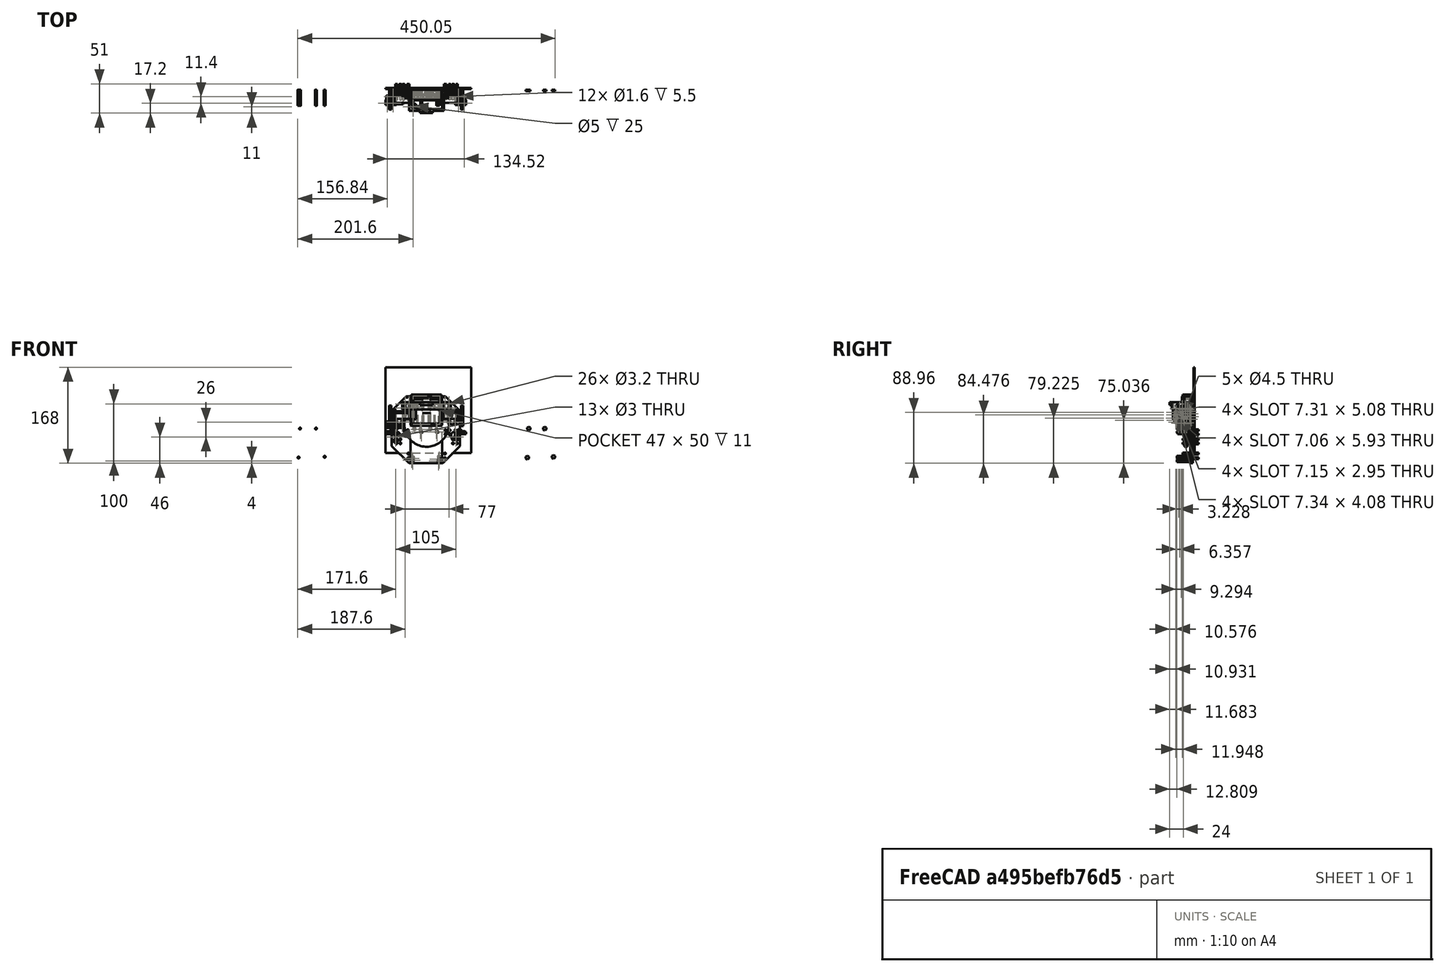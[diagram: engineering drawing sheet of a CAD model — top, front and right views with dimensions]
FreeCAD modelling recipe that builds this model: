
FCSTD DOCUMENT  (FreeCAD 0.17R13522 (Git))
Label: 5028.6 Frank
License: All rights reserved
LicenseURL: http://en.wikipedia.org/wiki/All_rights_reserved
objects: Part::Cylinder×153, Part::Fuse×90, Part::Box×86, Part::Cut×84, Part::Feature×37, Part::MultiFuse×35, Part::Fillet×28, Part::Chamfer×25, Part::Mirroring×16, Part::Cone×12, Part::Compound×3, Part::Torus×2, App::DocumentObjectGroup×1
note: 571 computed .brp shape members not serialized (recipe doc carries the construction recipe); baked Part::Feature solids carry a one-line shape summary decoded from their .brp

FEATURE [Part::Cylinder] Cylinder
  Angle = 360
  AttacherType = Attacher::AttachEngine3D
  Height = 30
  Radius = 7
FEATURE [Part::Cylinder] Cylinder001
  Angle = 360
  AttacherType = Attacher::AttachEngine3D
  Height = 19
  Placement = pos=(0,0,30) rot=(0,0,1;0rad)
  Radius = 7
FEATURE [Part::Cylinder] Cylinder002
  Angle = 360
  AttacherType = Attacher::AttachEngine3D
  Height = 1.8
  Placement = pos=(0,0,49) rot=(0,0,1;0rad)
  Radius = 2.5
FEATURE [Part::Compound] Compound
  Links = -> [Cylinder,Cylinder002,Cylinder001]
FEATURE [Part::Cylinder] Cylinder003
  Angle = 360
  AttacherType = Attacher::AttachEngine3D
  Height = 30
  Radius = 7
FEATURE [Part::Cylinder] Cylinder004
  Angle = 360
  AttacherType = Attacher::AttachEngine3D
  Height = 19
  Placement = pos=(0,0,30) rot=(0,0,1;0rad)
  Radius = 7
FEATURE [Part::Cylinder] Cylinder005
  Angle = 360
  AttacherType = Attacher::AttachEngine3D
  Height = 1.8
  Placement = pos=(0,0,49) rot=(0,0,1;0rad)
  Radius = 2.5
FEATURE [Part::Compound] Compound001
  Links = -> [Cylinder003,Cylinder005,Cylinder004]
  Placement = pos=(14.5,0,50) rot=(1,0,0;3.14159rad)
FEATURE [Part::Cylinder] Cylinder006
  Angle = 360
  AttacherType = Attacher::AttachEngine3D
  Height = 30
  Radius = 7
FEATURE [Part::Cylinder] Cylinder007
  Angle = 360
  AttacherType = Attacher::AttachEngine3D
  Height = 19
  Placement = pos=(0,0,30) rot=(0,0,1;0rad)
  Radius = 7
FEATURE [Part::Cylinder] Cylinder008
  Angle = 360
  AttacherType = Attacher::AttachEngine3D
  Height = 1.8
  Placement = pos=(0,0,49) rot=(0,0,1;0rad)
  Radius = 2.5
FEATURE [Part::Compound] Compound002
  Links = -> [Cylinder006,Cylinder008,Cylinder007]
  Placement = pos=(29,0,0) rot=(0,0,1;0rad)
FEATURE [Part::Box] Box  label="Cube"
  AttacherType = Attacher::AttachEngine3D
  Height = 50
  Length = 47
  Placement = pos=(-9,-8,0) rot=(0,0,1;0rad)
  Width = 12
FEATURE [Part::Box] Box001  label="Cube001"
  AttacherType = Attacher::AttachEngine3D
  Height = 55
  Length = 53
  Placement = pos=(-12,-8,-2.5) rot=(0,0,1;0rad)
  Width = 11
FEATURE [Part::Cylinder] Cylinder009
  Angle = 360
  AttacherType = Attacher::AttachEngine3D
  Height = 50
  Radius = 7
FEATURE [Part::Cylinder] Cylinder010
  Angle = 360
  AttacherType = Attacher::AttachEngine3D
  Height = 50
  Placement = pos=(14.5,0,0) rot=(0,0,1;0rad)
  Radius = 7
FEATURE [Part::Cut] Cut
  Base = -> Box001
  Tool = -> Box
FEATURE [Part::Box] Box002  label="Cube002"
  AttacherType = Attacher::AttachEngine3D
  Height = 55
  Length = 53
  Placement = pos=(-12,3,-2.5) rot=(0,0,1;0rad)
  Width = 7
FEATURE [Part::Fuse] Fusion
  Base = -> Cut
  Tool = -> Box002
FEATURE [Part::Cut] Cut001  label="No idea why this is here...."
  Base = -> Fusion
  Tool = -> Cylinder009
FEATURE [Part::Cylinder] Cylinder011
  Angle = 360
  AttacherType = Attacher::AttachEngine3D
  Height = 50
  Placement = pos=(29,0,0) rot=(0,0,1;0rad)
  Radius = 7
FEATURE [Part::Box] Box003  label="Cube003"
  AttacherType = Attacher::AttachEngine3D
  Height = 5
  Length = 2
  Placement = pos=(28,-9,-2) rot=(0,0,1;0rad)
  Width = 12
FEATURE [Part::Box] Box004  label="Cube004"
  AttacherType = Attacher::AttachEngine3D
  Height = 5
  Length = 2
  Placement = pos=(18.5,-9,46) rot=(0,0,1;0rad)
  Width = 12
FEATURE [Part::Box] Box005  label="Cube005"
  AttacherType = Attacher::AttachEngine3D
  Height = 5
  Length = 2
  Placement = pos=(-2,-9,46) rot=(0,0,1;0rad)
  Width = 12
FEATURE [Part::Box] Box006  label="Cube006"
  AttacherType = Attacher::AttachEngine3D
  Height = 5
  Length = 3
  Placement = pos=(35,-9,-4) rot=(0,0,1;0rad)
  Width = 12
FEATURE [Part::Cut] Cut008
FEATURE [Part::Torus] Torus001
  Angle1 = -180
  Angle2 = 180
  Angle3 = 360
  AttacherType = Attacher::AttachEngine3D
  Placement = pos=(0,0,2) rot=(0,0,1;0rad)
  Radius1 = 19
  Radius2 = 1.5
FEATURE [Part::Cut] Cut009  label="wheel2"
  Base = -> Cut008
  Placement = pos=(75,-7,15) rot=(0,1,0;1.5708rad)
  Tool = -> Torus001
FEATURE [Part::Torus] Torus
  Angle1 = -180
  Angle2 = 180
  Angle3 = 360
  AttacherType = Attacher::AttachEngine3D
  Placement = pos=(0,0,2) rot=(0,0,1;0rad)
  Radius1 = 19
  Radius2 = 1.5
FEATURE [Part::Cut] Cut010
FEATURE [Part::Cut] Cut011  label="wheel1"
  Base = -> Cut010
  Placement = pos=(-51,-7,15) rot=(0,1,0;1.5708rad)
  Tool = -> Torus
FEATURE [Part::Fuse] Fusion003
FEATURE [Part::Cylinder] Cylinder012
  Angle = 360
  AttacherType = Attacher::AttachEngine3D
  Height = 10
  Placement = pos=(5,-4.5,0) rot=(0,1,0;1.5708rad)
  Radius = 0.8
FEATURE [Part::Fuse] Fusion048  label="right-motor001"
  Base = -> Cylinder012
  Placement = pos=(-51,-7,15) rot=(0,0,1;0rad)
  Tool = -> Fusion003
FEATURE [Part::Fuse] Fusion049
FEATURE [Part::Cylinder] Cylinder013
  Angle = 360
  AttacherType = Attacher::AttachEngine3D
  Height = 10
  Placement = pos=(5,-4.5,0) rot=(0,1,0;1.5708rad)
  Radius = 0.8
FEATURE [Part::Fuse] Fusion050  label="left-motor001"
  Base = -> Cylinder013
  Placement = pos=(79,-7,15) rot=(0,0,1;3.14159rad)
  Tool = -> Fusion049
FEATURE [Part::Box] Box007  label="Cube007"
  AttacherType = Attacher::AttachEngine3D
  Height = 5
  Length = 2
  Placement = pos=(37.5,-9,46) rot=(0,0,1;0rad)
  Width = 12
FEATURE [Part::Box] Box008  label="Cube008"
  AttacherType = Attacher::AttachEngine3D
  Height = 5
  Length = 2
  Placement = pos=(8,-9,-2) rot=(0,0,1;0rad)
  Width = 12
FEATURE [Part::Box] Box009  label="The Ground"
  AttacherType = Attacher::AttachEngine3D
  Height = 150
  Length = 150
  Placement = pos=(-57,11,-50) rot=(0,0,1;0rad)
  Width = 2
FEATURE [Part::Box] Box010  label="Motor Mount Left"
  AttacherType = Attacher::AttachEngine3D
  Height = 16
  Length = 4
  Placement = pos=(69,-13,7) rot=(0,0,1;0rad)
  Width = 20
FEATURE [Part::Box] Box011  label="Motor Mount Right"
  AttacherType = Attacher::AttachEngine3D
  Height = 16
  Length = 4
  Placement = pos=(-46,-13,7) rot=(0,0,1;0rad)
  Width = 20
FEATURE [Part::Box] Box012  label="Motor Support Right"
  AttacherType = Attacher::AttachEngine3D
  Height = 16
  Length = 10
  Placement = pos=(-25,-1,7) rot=(0,0,1;0rad)
  Width = 8
FEATURE [Part::Box] Box013  label="Motor Support Left"
  AttacherType = Attacher::AttachEngine3D
  Height = 16
  Length = 10
  Placement = pos=(43,-1,7) rot=(0,0,1;0rad)
  Width = 8
FEATURE [Part::Cylinder] Cylinder014
  Angle = 360
  AttacherType = Attacher::AttachEngine3D
  Height = 28
  Placement = pos=(40.7,0,-10.3) rot=(1,0,0;1.5708rad)
  Radius = 1.6
FEATURE [Part::Cylinder] Cylinder015
  Angle = 360
  AttacherType = Attacher::AttachEngine3D
  Height = 28
  Placement = pos=(-2.4,0,-59.8) rot=(1,0,0;1.5708rad)
  Radius = 1.6
FEATURE [Part::Cylinder] Cylinder016
  Angle = 360
  AttacherType = Attacher::AttachEngine3D
  Height = 28
  Placement = pos=(-5,0,-9) rot=(1,0,0;1.5708rad)
  Radius = 1.6
FEATURE [Part::Cylinder] Cylinder017
  Angle = 360
  AttacherType = Attacher::AttachEngine3D
  Height = 28
  Placement = pos=(25.5,0,-59.8) rot=(1,0,0;1.5708rad)
  Radius = 1.6
FEATURE [Part::Fuse] Fusion051
  Base = -> Cylinder015
  Tool = -> Cylinder016
FEATURE [Part::Fuse] Fusion052
  Base = -> Cylinder014
  Tool = -> Cylinder017
FEATURE [Part::Fuse] Fusion053  label="Screw holes on Arduino Duo"
  Base = -> Fusion051
  Tool = -> Fusion052
FEATURE [Part::Mirroring] Part__Mirroring  label="XXXXXScrew holes on Arduino Duo (Mirror #1)"
  Base = (0,0,0)
  Normal = (0,0,1)
  Placement = pos=(-204,10,-67) rot=(0,0,1;0rad)
  Source = -> Fusion053
FEATURE [Part::Box] Box014  label="Not used Cube"
  AttacherType = Attacher::AttachEngine3D
  Height = 10
  Length = 10
  Placement = pos=(-1,4,-5.85) rot=(0,0,1;0rad)
  Width = 10
FEATURE [Part::Box] Box015  label="Cube014 Arduino Support cube"
  AttacherType = Attacher::AttachEngine3D
  Height = 67
  Length = 55
  Placement = pos=(-13,5,-68) rot=(0,0,1;0rad)
  Width = 5
FEATURE [Part::Cylinder] Cylinder018
  Angle = 360
  AttacherType = Attacher::AttachEngine3D
  Height = 5
  Placement = pos=(15,0,0) rot=(1,0,0;1.5708rad)
  Radius = 39
FEATURE [Part::Cut] Cut014  label="M3 Nut"
  Base = -> Cut001
  Placement = pos=(-6.4,10,-7.2) rot=(1,0,0;1.5708rad)
  Tool = -> Cylinder001
FEATURE [Part::Cut] Cut015  label="M3 Nut001"
  Base = -> Cut001
  Placement = pos=(21.5,10,-7.2) rot=(1,0,0;1.5708rad)
  Tool = -> Cylinder001
FEATURE [Part::Cut] Cut016  label="M3 Nut002"
  Base = -> Cut001
  Placement = pos=(36.7,10,-56.7) rot=(1,0,0;1.5708rad)
  Tool = -> Cylinder001
FEATURE [Part::Cut] Cut017  label="M3 Nut003"
  Base = -> Cut001
  Placement = pos=(-9,10,-58) rot=(1,0,0;1.5708rad)
  Tool = -> Cylinder001
FEATURE [Part::Cut] Cut018
  Base = -> Cut
  Placement = pos=(-9,10,-58) rot=(1,0,0;1.5708rad)
  Tool = -> Box006
FEATURE [Part::Cut] Cut019
  Base = -> Cut
  Placement = pos=(36.7,10,-56.7) rot=(1,0,0;1.5708rad)
  Tool = -> Box006
FEATURE [Part::Cut] Cut020
  Base = -> Cut
  Placement = pos=(-6.4,10,-7.2) rot=(1,0,0;1.5708rad)
  Tool = -> Box006
FEATURE [Part::Cut] Cut021
  Base = -> Cut
  Placement = pos=(21.5,10,-7.2) rot=(1,0,0;1.5708rad)
  Tool = -> Box006
FEATURE [Part::MultiFuse] Fusion054  label="XXXXXHex Holes"
  Placement = pos=(200,0,0) rot=(0,0,1;0rad)
  Shapes = -> [Cut018,Cut021,Cut019,Cut020]
FEATURE [Part::Box] Box016  label="Cube015"
  AttacherType = Attacher::AttachEngine3D
  Height = 117
  Length = 33
  Placement = pos=(-46,7,-68) rot=(0,0,1;0rad)
  Width = 3
FEATURE [Part::Box] Box017  label="Cube016"
  AttacherType = Attacher::AttachEngine3D
  Height = 117
  Length = 31
  Placement = pos=(42,7,-68) rot=(0,0,1;0rad)
  Width = 3
FEATURE [Part::Cylinder] Cylinder019
  Angle = 360
  AttacherType = Attacher::AttachEngine3D
  Height = 28
  Placement = pos=(48,20,-10) rot=(1,0,0;1.5708rad)
  Radius = 1.6
FEATURE [Part::Cylinder] Cylinder020
  Angle = 360
  AttacherType = Attacher::AttachEngine3D
  Height = 28
  Placement = pos=(47,20,-51) rot=(1,0,0;1.5708rad)
  Radius = 1.6
FEATURE [Part::Cylinder] Cylinder021
  Angle = 360
  AttacherType = Attacher::AttachEngine3D
  Height = 28
  Placement = pos=(48,20,-17) rot=(1,0,0;1.5708rad)
  Radius = 1.6
FEATURE [Part::Cylinder] Cylinder022
  Angle = 360
  AttacherType = Attacher::AttachEngine3D
  Height = 28
  Placement = pos=(47,20,-59) rot=(1,0,0;1.5708rad)
  Radius = 1.6
FEATURE [Part::Cylinder] Cylinder023
  Angle = 360
  AttacherType = Attacher::AttachEngine3D
  Height = 28
  Placement = pos=(55,20,-17) rot=(1,0,0;1.5708rad)
  Radius = 1.6
FEATURE [Part::Cylinder] Cylinder024
  Angle = 360
  AttacherType = Attacher::AttachEngine3D
  Height = 28
  Placement = pos=(55,20,-10) rot=(1,0,0;1.5708rad)
  Radius = 1.6
FEATURE [Part::MultiFuse] Fusion055
  Shapes = -> [Cylinder021,Cylinder023,Cylinder024,Cylinder019]
FEATURE [Part::MultiFuse] Fusion056
  Placement = pos=(13,0,-16) rot=(0,0,1;0rad)
  Shapes = -> [Cylinder021,Cylinder023,Cylinder024,Cylinder019]
FEATURE [Part::MultiFuse] Fusion057  label="Mount holes top left"
  Placement = pos=(-1,0,46) rot=(0,0,1;0rad)
  Shapes = -> [Cylinder021,Cylinder023,Cylinder024,Cylinder019]
FEATURE [Part::MultiFuse] Fusion058  label="Mount holes top right"
  Placement = pos=(-71,0,46) rot=(0,0,1;0rad)
  Shapes = -> [Cylinder021,Cylinder023,Cylinder024,Cylinder019]
FEATURE [Part::MultiFuse] Fusion059
  Shapes = -> [Cylinder022,Cylinder020,Fusion055,Fusion056]
FEATURE [Part::Mirroring] Part__Mirroring001  label="Mount holes bottom right"
  Base = (0,0,0)
  Normal = (1,0,0)
  Placement = pos=(30,0,0) rot=(0,0,1;0rad)
  Source = -> Fusion059
FEATURE [Part::Cylinder] Cylinder025
  Angle = 360
  AttacherType = Attacher::AttachEngine3D
  Height = 28
  Placement = pos=(48,20,-10) rot=(1,0,0;1.5708rad)
  Radius = 1.6
FEATURE [Part::Cylinder] Cylinder026
  Angle = 360
  AttacherType = Attacher::AttachEngine3D
  Height = 28
  Placement = pos=(47,20,-51) rot=(1,0,0;1.5708rad)
  Radius = 1.6
FEATURE [Part::Cylinder] Cylinder027
  Angle = 360
  AttacherType = Attacher::AttachEngine3D
  Height = 28
  Placement = pos=(48,20,-17) rot=(1,0,0;1.5708rad)
  Radius = 1.6
FEATURE [Part::Cylinder] Cylinder028
  Angle = 360
  AttacherType = Attacher::AttachEngine3D
  Height = 28
  Placement = pos=(47,20,-59) rot=(1,0,0;1.5708rad)
  Radius = 1.6
FEATURE [Part::Cylinder] Cylinder029
  Angle = 360
  AttacherType = Attacher::AttachEngine3D
  Height = 28
  Placement = pos=(55,20,-17) rot=(1,0,0;1.5708rad)
  Radius = 1.6
FEATURE [Part::Cylinder] Cylinder030
  Angle = 360
  AttacherType = Attacher::AttachEngine3D
  Height = 28
  Placement = pos=(55,20,-10) rot=(1,0,0;1.5708rad)
  Radius = 1.6
FEATURE [Part::MultiFuse] Fusion060
  Shapes = -> [Cylinder027,Cylinder029,Cylinder030,Cylinder025]
FEATURE [Part::MultiFuse] Fusion061
  Placement = pos=(13,0,-16) rot=(0,0,1;0rad)
  Shapes = -> [Cylinder027,Cylinder029,Cylinder030,Cylinder025]
FEATURE [Part::MultiFuse] Fusion062  label="Mount holes bottom left"
  Shapes = -> [Cylinder028,Cylinder026,Fusion060,Fusion061]
FEATURE [Part::Cylinder] Cylinder031  label="Cylinder127"
  Angle = 360
  AttacherType = Attacher::AttachEngine3D
  Height = 10
  Placement = pos=(0,18,29) rot=(0,0,1;0rad)
  Radius = 2.25
FEATURE [Part::Cylinder] Cylinder032  label="Cylinder128"
  Angle = 360
  AttacherType = Attacher::AttachEngine3D
  Height = 10
  Placement = pos=(4.5,18,32) rot=(0,0,1;0rad)
  Radius = 1
FEATURE [Part::Cylinder] Cylinder033  label="Cylinder129"
  Angle = 360
  AttacherType = Attacher::AttachEngine3D
  Height = 10
  Placement = pos=(-4.5,18,32) rot=(0,0,1;0rad)
  Radius = 1
FEATURE [Part::Fuse] Fusion009  label="Mounting Screw Holes"
  Base = -> Cylinder032
  Tool = -> Cylinder033
FEATURE [Part::Fuse] Fusion071  label="Motor Holes Left"
  Base = -> Cylinder031
  Placement = pos=(37,-7,-3) rot=(0.57735,0.57735,0.57735;2.0944rad)
  Tool = -> Fusion009
FEATURE [Part::Cylinder] Cylinder034  label="Cylinder130"
  Angle = 360
  AttacherType = Attacher::AttachEngine3D
  Height = 10
  Placement = pos=(0,18,29) rot=(0,0,1;0rad)
  Radius = 2.25
FEATURE [Part::Cylinder] Cylinder035  label="Cylinder131"
  Angle = 360
  AttacherType = Attacher::AttachEngine3D
  Height = 10
  Placement = pos=(4.5,18,32) rot=(0,0,1;0rad)
  Radius = 1
FEATURE [Part::Cylinder] Cylinder036  label="Cylinder132"
  Angle = 360
  AttacherType = Attacher::AttachEngine3D
  Height = 10
  Placement = pos=(-4.5,18,32) rot=(0,0,1;0rad)
  Radius = 1
FEATURE [Part::Fuse] Fusion072  label="Mounting Screw Holes001"
  Base = -> Cylinder035
  Tool = -> Cylinder036
FEATURE [Part::Fuse] Fusion073  label="Motor Holes Right"
  Base = -> Cylinder034
  Placement = pos=(-79,-7,-3) rot=(0.57735,0.57735,0.57735;2.0944rad)
  Tool = -> Fusion072
FEATURE [Part::Cylinder] Cylinder037  label="Cylinder133"
  Angle = 360
  AttacherType = Attacher::AttachEngine3D
  Height = 28
  Placement = pos=(40.7,0,-10.3) rot=(1,0,0;1.5708rad)
  Radius = 1.6
FEATURE [Part::Cylinder] Cylinder038  label="Cylinder134"
  Angle = 360
  AttacherType = Attacher::AttachEngine3D
  Height = 28
  Placement = pos=(-2.4,0,-59.8) rot=(1,0,0;1.5708rad)
  Radius = 1.6
FEATURE [Part::Cylinder] Cylinder039  label="Cylinder135"
  Angle = 360
  AttacherType = Attacher::AttachEngine3D
  Height = 28
  Placement = pos=(-5,0,-9) rot=(1,0,0;1.5708rad)
  Radius = 1.6
FEATURE [Part::Cylinder] Cylinder040  label="Cylinder136"
  Angle = 360
  AttacherType = Attacher::AttachEngine3D
  Height = 28
  Placement = pos=(25.5,0,-59.8) rot=(1,0,0;1.5708rad)
  Radius = 1.6
FEATURE [Part::Fuse] Fusion074
  Base = -> Cylinder038
  Tool = -> Cylinder039
FEATURE [Part::Fuse] Fusion075
  Base = -> Cylinder037
  Tool = -> Cylinder040
FEATURE [Part::Fuse] Fusion076  label="Screw holes on Arduino Duo001"
  Base = -> Fusion074
  Tool = -> Fusion075
FEATURE [Part::Mirroring] Part__Mirroring002  label="Screw holes on Arduino Duo (Mirror #1)001"
  Base = (0,0,0)
  Normal = (0,0,1)
  Placement = pos=(-4,10,-67) rot=(0,0,1;0rad)
  Source = -> Fusion076
FEATURE [Part::Mirroring] Part__Mirroring003  label="Screw holes on Arduino Duo (Mirror #1)001 (Mirror #4)"
  Base = (0,0,0)
  Normal = (1,0,0)
  Placement = pos=(27,0,-6) rot=(0,0,1;0rad)
  Source = -> Part__Mirroring002
FEATURE [Part::Box] Box018  label="Cube017"
  AttacherType = Attacher::AttachEngine3D
  Height = 50
  Length = 47
  Placement = pos=(-9,-8,0) rot=(0,0,1;0rad)
  Width = 12
FEATURE [Part::Box] Box019  label="Cube018"
  AttacherType = Attacher::AttachEngine3D
  Height = 55
  Length = 53
  Placement = pos=(-12,-8,-2.5) rot=(0,0,1;0rad)
  Width = 11
FEATURE [Part::Cut] Cut031
  Base = -> Box019
  Tool = -> Box018
FEATURE [Part::Box] Box020  label="Cube019"
  AttacherType = Attacher::AttachEngine3D
  Height = 5
  Length = 3
  Placement = pos=(35,-9,-4) rot=(0,0,1;0rad)
  Width = 12
FEATURE [Part::Cut] Cut032
  Base = -> Cut031
  Placement = pos=(-9,10,-58) rot=(1,0,0;1.5708rad)
  Tool = -> Box020
FEATURE [Part::Cut] Cut033
  Base = -> Cut031
  Placement = pos=(36.7,10,-56.7) rot=(1,0,0;1.5708rad)
  Tool = -> Box020
FEATURE [Part::Cut] Cut034
  Base = -> Cut031
  Placement = pos=(-6.4,10,-7.2) rot=(1,0,0;1.5708rad)
  Tool = -> Box020
FEATURE [Part::Cut] Cut035
  Base = -> Cut031
  Placement = pos=(21.5,10,-7.2) rot=(1,0,0;1.5708rad)
  Tool = -> Box020
FEATURE [Part::MultiFuse] Fusion077
  Shapes = -> [Cut032,Cut035,Cut033,Cut034]
FEATURE [Part::Mirroring] Part__Mirroring004  label="Hex Holes"
  Base = (0,0,0)
  Normal = (1,0,0)
  Placement = pos=(27,0,-6) rot=(0,0,1;0rad)
  Source = -> Fusion077
FEATURE [Part::Box] Box021  label="Cube020"
  AttacherType = Attacher::AttachEngine3D
  Height = 13
  Length = 61
  Placement = pos=(-16,-27,26) rot=(0,0,1;0rad)
  Width = 34
FEATURE [Part::Box] Box022  label="Cube021"
  AttacherType = Attacher::AttachEngine3D
  Height = 13
  Length = 12
  Placement = pos=(45,4,26) rot=(0,0,1;0rad)
  Width = 3
FEATURE [Part::Box] Box023  label="Cube022"
  AttacherType = Attacher::AttachEngine3D
  Height = 13
  Length = 12
  Placement = pos=(-28,4,26) rot=(0,0,1;0rad)
  Width = 3
FEATURE [Part::Box] Box024  label="Cube023"
  AttacherType = Attacher::AttachEngine3D
  Height = 13
  Length = 55
  Placement = pos=(-13,-24,26) rot=(0,0,1;0rad)
  Width = 31
FEATURE [Part::Cylinder] Cylinder041  label="Cylinder137"
  Angle = 360
  AttacherType = Attacher::AttachEngine3D
  Height = 28
  Placement = pos=(54,20,29) rot=(1,0,0;1.5708rad)
  Radius = 1.6
FEATURE [Part::Cylinder] Cylinder042  label="Cylinder138"
  Angle = 360
  AttacherType = Attacher::AttachEngine3D
  Height = 28
  Placement = pos=(54,20,36) rot=(1,0,0;1.5708rad)
  Radius = 1.6
FEATURE [Part::Cylinder] Cylinder043  label="Cylinder139"
  Angle = 360
  AttacherType = Attacher::AttachEngine3D
  Height = 28
  Placement = pos=(-23,20,29) rot=(1,0,0;1.5708rad)
  Radius = 1.6
FEATURE [Part::Cylinder] Cylinder044  label="Cylinder140"
  Angle = 360
  AttacherType = Attacher::AttachEngine3D
  Height = 28
  Placement = pos=(-23,20,36) rot=(1,0,0;1.5708rad)
  Radius = 1.6
FEATURE [Part::Cylinder] Cylinder045  label="Cylinder141"
  Angle = 360
  AttacherType = Attacher::AttachEngine3D
  Height = 10
  Placement = pos=(36,-17.25,32.5) rot=(0,1,0;1.5708rad)
  Radius = 2.5
FEATURE [Part::Cut] Cut037
  Base = -> Box021
  Tool = -> Box024
FEATURE [Part::Cut] Cut038
  Base = -> Cut037
  Tool = -> Cylinder045
FEATURE [Part::Box] Box025  label="Cube024"
  AttacherType = Attacher::AttachEngine3D
  Height = 5
  Length = 22
  Placement = pos=(3.5,-31,34) rot=(0,0,1;0rad)
  Width = 4
FEATURE [Part::Cylinder] Cylinder046  label="Cylinder142"
  Angle = 360
  AttacherType = Attacher::AttachEngine3D
  Height = 10
  Placement = pos=(20.75,-29,30) rot=(0,0,1;0rad)
  Radius = 0.85
FEATURE [Part::Cylinder] Cylinder047  label="Cylinder143"
  Angle = 360
  AttacherType = Attacher::AttachEngine3D
  Height = 10
  Placement = pos=(8.25,-29,40) rot=(1,0,0;3.14159rad)
  Radius = 0.85
FEATURE [Part::Fuse] Fusion078
  Base = -> Cylinder046
  Tool = -> Cylinder047
FEATURE [Part::Cut] Cut039
  Base = -> Box025
  Tool = -> Fusion078
FEATURE [Part::Fuse] Fusion079
  Base = -> Cut038
  Tool = -> Cut039
FEATURE [Part::Fuse] Fusion080
  Base = -> Cylinder043
  Tool = -> Cylinder044
FEATURE [Part::Fuse] Fusion081
  Base = -> Cylinder041
  Tool = -> Cylinder042
FEATURE [Part::Fuse] Fusion082
  Base = -> Box023
  Tool = -> Fusion079
FEATURE [Part::Fuse] Fusion083
  Base = -> Box022
  Tool = -> Fusion082
FEATURE [Part::Cut] Cut040
  Base = -> Fusion083
  Tool = -> Fusion081
FEATURE [Part::Cut] Cut041  label="Switch Bracket"
  Base = -> Cut040
  Tool = -> Fusion080
FEATURE [Part::Cylinder] Cylinder048  label="Cylinder144"
  Angle = 360
  AttacherType = Attacher::AttachEngine3D
  Height = 28
  Placement = pos=(-23,20,29) rot=(1,0,0;1.5708rad)
  Radius = 1.6
FEATURE [Part::Cylinder] Cylinder049  label="Cylinder145"
  Angle = 360
  AttacherType = Attacher::AttachEngine3D
  Height = 28
  Placement = pos=(-23,20,36) rot=(1,0,0;1.5708rad)
  Radius = 1.6
FEATURE [Part::Fuse] Fusion084
  Base = -> Cylinder048
  Placement = pos=(1,0,0) rot=(0,0,1;0rad)
  Tool = -> Cylinder049
FEATURE [Part::Cylinder] Cylinder050  label="Cylinder146"
  Angle = 360
  AttacherType = Attacher::AttachEngine3D
  Height = 28
  Placement = pos=(-23,20,29) rot=(1,0,0;1.5708rad)
  Radius = 1.6
FEATURE [Part::Cylinder] Cylinder051  label="Cylinder147"
  Angle = 360
  AttacherType = Attacher::AttachEngine3D
  Height = 28
  Placement = pos=(-23,20,36) rot=(1,0,0;1.5708rad)
  Radius = 1.6
FEATURE [Part::Fuse] Fusion085
  Base = -> Cylinder050
  Placement = pos=(-1,0,0) rot=(0,0,1;0rad)
  Tool = -> Cylinder051
FEATURE [Part::Cut] Cut042
  Base = -> Cut041
  Tool = -> Fusion084
FEATURE [Part::Cut] Cut043  label="Switch Bracket001"
  Base = -> Cut042
  Tool = -> Fusion085
FEATURE [Part::Cylinder] Cylinder052  label="Cylinder148"
  Angle = 360
  AttacherType = Attacher::AttachEngine3D
  Height = 42
  Radius = 4.8
FEATURE [Part::Cylinder] Cylinder053  label="Cylinder149"
  Angle = 360
  AttacherType = Attacher::AttachEngine3D
  Height = 1.6
  Placement = pos=(0,0,42) rot=(0,0,1;0rad)
  Radius = 1.65
FEATURE [Part::Fuse] Fusion086
  Base = -> Cylinder052
  Placement = pos=(2,0,0) rot=(0,0,1;0rad)
  Tool = -> Cylinder053
FEATURE [Part::Cylinder] Cylinder054  label="Cylinder150"
  Angle = 360
  AttacherType = Attacher::AttachEngine3D
  Height = 42
  Radius = 4.8
FEATURE [Part::Cylinder] Cylinder055  label="Cylinder151"
  Angle = 360
  AttacherType = Attacher::AttachEngine3D
  Height = 1.6
  Placement = pos=(0,0,42) rot=(0,0,1;0rad)
  Radius = 1.65
FEATURE [Part::Fuse] Fusion087
  Base = -> Cylinder054
  Placement = pos=(12,0,0) rot=(0,0,1;0rad)
  Tool = -> Cylinder055
FEATURE [Part::Cylinder] Cylinder056  label="Cylinder152"
  Angle = 360
  AttacherType = Attacher::AttachEngine3D
  Height = 42
  Radius = 4.8
FEATURE [Part::Cylinder] Cylinder057  label="Cylinder153"
  Angle = 360
  AttacherType = Attacher::AttachEngine3D
  Height = 1.6
  Placement = pos=(0,0,42) rot=(0,0,1;0rad)
  Radius = 1.65
FEATURE [Part::Fuse] Fusion088
  Base = -> Cylinder056
  Placement = pos=(22,0,0) rot=(0,0,1;0rad)
  Tool = -> Cylinder057
FEATURE [Part::Cylinder] Cylinder058  label="Cylinder154"
  Angle = 360
  AttacherType = Attacher::AttachEngine3D
  Height = 42
  Radius = 4.8
FEATURE [Part::Cylinder] Cylinder059  label="Cylinder155"
  Angle = 360
  AttacherType = Attacher::AttachEngine3D
  Height = 1.6
  Placement = pos=(0,0,42) rot=(0,0,1;0rad)
  Radius = 1.65
FEATURE [Part::Fuse] Fusion089
  Base = -> Cylinder058
  Placement = pos=(32,0,0) rot=(0,0,1;0rad)
  Tool = -> Cylinder059
FEATURE [Part::Cylinder] Cylinder060  label="Cylinder156"
  Angle = 360
  AttacherType = Attacher::AttachEngine3D
  Height = 42
  Radius = 4.8
FEATURE [Part::Cylinder] Cylinder061  label="Cylinder157"
  Angle = 360
  AttacherType = Attacher::AttachEngine3D
  Height = 1.6
  Placement = pos=(0,0,42) rot=(0,0,1;0rad)
  Radius = 1.65
FEATURE [Part::Fuse] Fusion093
  Base = -> Cylinder060
  Placement = pos=(-8,0,0) rot=(0,0,1;0rad)
  Tool = -> Cylinder061
FEATURE [Part::MultiFuse] Fusion094  label="AAA Batts"
  Placement = pos=(2.5,0,2) rot=(0,0,1;0rad)
  Shapes = -> [Fusion093,Fusion086,Fusion087,Fusion088,Fusion089]
FEATURE [Part::Cylinder] Cylinder062  label="Cylinder158"
  Angle = 360
  AttacherType = Attacher::AttachEngine3D
  Height = 10
  Radius = 17
FEATURE [Part::Cylinder] Cylinder063  label="Cylinder159"
  Angle = 360
  AttacherType = Attacher::AttachEngine3D
  Height = 16
  Placement = pos=(0,0,-4) rot=(0,0,1;0rad)
  Radius = 10
FEATURE [Part::Cut] Cut044
  Base = -> Cylinder062
  Tool = -> Cylinder063
FEATURE [Part::Box] Box026  label="Cube025"
  AttacherType = Attacher::AttachEngine3D
  Height = 20
  Length = 18
  Placement = pos=(0,0,-5) rot=(0,0,1;0rad)
  Width = 20
FEATURE [Part::Box] Box027  label="Cube026"
  AttacherType = Attacher::AttachEngine3D
  Height = 20
  Length = 10
  Placement = pos=(0,0,-5) rot=(0,0,1;0.174533rad)
  Width = 20
FEATURE [Part::Cut] Cut045
  Base = -> Box027
  Tool = -> Box026
FEATURE [Part::Feature] Cut045001
  Placement = pos=(0,0,0) rot=(0,0,1;0.349066rad)
  shape: bbox 10 x 22.32 x 20 mm, 7 faces (baked)
FEATURE [Part::Feature] Cut045002
  Placement = pos=(0,0,0) rot=(0,0,1;0.698132rad)
  shape: bbox 15.32 x 20.52 x 20 mm, 7 faces (baked)
FEATURE [Part::Feature] Cut045003
  Placement = pos=(0,0,0) rot=(0,0,1;1.0472rad)
  shape: bbox 18.79 x 16.24 x 20 mm, 7 faces (baked)
FEATURE [Part::Feature] Cut045004
  Placement = pos=(0,0,0) rot=(0,0,1;1.39626rad)
  shape: bbox 20 x 10 x 20 mm, 7 faces (baked)
FEATURE [Part::Feature] Cut045005
  Placement = pos=(0,0,0) rot=(0,0,1;1.74533rad)
  shape: bbox 22.21 x 9.894 x 20 mm, 7 faces (baked)
FEATURE [Part::Feature] Cut045006
  Placement = pos=(0,0,0) rot=(0,0,1;2.0944rad)
  shape: bbox 21.75 x 12.86 x 20 mm, 7 faces (baked)
FEATURE [Part::Feature] Cut045007
  Placement = pos=(0,0,0) rot=(0,0,1;2.44346rad)
  shape: bbox 18.66 x 17.32 x 20 mm, 7 faces (baked)
FEATURE [Part::Feature] Cut045008
  Placement = pos=(0,0,0) rot=(0,0,1;2.79253rad)
  shape: bbox 13.32 x 19.7 x 20 mm, 7 faces (baked)
FEATURE [Part::Feature] Cut045009
  Placement = pos=(0,0,0) rot=(0,0,1;3.14159rad)
  shape: bbox 10.1 x 21.43 x 20 mm, 7 faces (baked)
FEATURE [Part::Feature] Cut045010
  Placement = pos=(0,0,0) rot=(0,0,1;3.49066rad)
  shape: bbox 10 x 22.32 x 20 mm, 7 faces (baked)
FEATURE [Part::Feature] Cut045011
  Placement = pos=(0,0,0) rot=(0,0,1;3.83972rad)
  shape: bbox 15.32 x 20.52 x 20 mm, 7 faces (baked)
FEATURE [Part::Feature] Cut045012
  Placement = pos=(0,0,0) rot=(0,0,1;4.18879rad)
  shape: bbox 18.79 x 16.24 x 20 mm, 7 faces (baked)
FEATURE [Part::Feature] Cut045013
  Placement = pos=(0,0,0) rot=(0,0,-1;1.74533rad)
  shape: bbox 20 x 10 x 20 mm, 7 faces (baked)
FEATURE [Part::Feature] Cut045014
  Placement = pos=(0,0,0) rot=(0,0,-1;1.39626rad)
  shape: bbox 22.21 x 9.894 x 20 mm, 7 faces (baked)
FEATURE [Part::Feature] Cut045015
  Placement = pos=(0,0,0) rot=(0,0,-1;1.0472rad)
  shape: bbox 21.75 x 12.86 x 20 mm, 7 faces (baked)
FEATURE [Part::Feature] Cut045016
  Placement = pos=(0,0,0) rot=(0,0,-1;0.698132rad)
  shape: bbox 18.66 x 17.32 x 20 mm, 7 faces (baked)
FEATURE [Part::Feature] Cut045017
  Placement = pos=(0,0,0) rot=(0,0,-1;0.349066rad)
  shape: bbox 13.32 x 19.7 x 20 mm, 7 faces (baked)
FEATURE [Part::MultiFuse] Fusion095
  Shapes = -> [Cut045001,Cut045008,Cut045010,Cut045009,Cut045005,Cut045003,Cut045006,Cut045002,Cut045004,Cut045007,Cut045016,Cut045017,Cut045011,Cut045012,Cut045013,Cut045014,Cut045015,Cut045]
FEATURE [Part::Cut] Cut045018
  Base = -> Cut044
  Placement = pos=(72,-7,15) rot=(0,1,0;1.5708rad)
  Tool = -> Fusion095
FEATURE [Part::Cut] Cut045019  label="Wheel with Spokes AB"
  Base = -> Cut009
  Tool = -> Cut045018
FEATURE [Part::Box] Box028  label="Cube027"
  AttacherType = Attacher::AttachEngine3D
  Height = 5
  Length = 2
  Placement = pos=(37.5,-9,-2) rot=(0,0,1;0rad)
  Width = 12
FEATURE [Part::Box] Box029  label="Cube028"
  AttacherType = Attacher::AttachEngine3D
  Height = 50
  Length = 47
  Placement = pos=(-9,-8,0) rot=(0,0,1;0rad)
  Width = 12
FEATURE [Part::Box] Box030  label="Cube029"
  AttacherType = Attacher::AttachEngine3D
  Height = 55
  Length = 53
  Placement = pos=(-12,-8,-2.5) rot=(0,0,1;0rad)
  Width = 11
FEATURE [Part::Cylinder] Cylinder064  label="Cylinder160"
  Angle = 360
  AttacherType = Attacher::AttachEngine3D
  Height = 50
  Radius = 7
FEATURE [Part::Cut] Cut045020
  Base = -> Box030
  Tool = -> Box029
FEATURE [Part::Box] Box031  label="Cube030"
  AttacherType = Attacher::AttachEngine3D
  Height = 55
  Length = 53
  Placement = pos=(-12,3,-2.5) rot=(0,0,1;0rad)
  Width = 7
FEATURE [Part::Fuse] Fusion096
  Base = -> Cut045020
  Tool = -> Box031
FEATURE [Part::Box] Box032  label="Battery Base"
  AttacherType = Attacher::AttachEngine3D
  Height = 50
  Length = 55
  Placement = pos=(-13,3,-1) rot=(0,0,1;0rad)
  Width = 7
FEATURE [Part::Box] Box033  label="Cube031"
  AttacherType = Attacher::AttachEngine3D
  Height = 30
  Length = 10
  Placement = pos=(-14,-25,9) rot=(0,0,1;0rad)
  Width = 10
FEATURE [Part::Cylinder] Cylinder065  label="Cylinder161"
  Angle = 360
  AttacherType = Attacher::AttachEngine3D
  Height = 43.5
  Placement = pos=(4,0,2) rot=(0,0,1;0rad)
  Radius = 4.8
FEATURE [Part::Cylinder] Cylinder066  label="Cylinder162"
  Angle = 360
  AttacherType = Attacher::AttachEngine3D
  Height = 1.6
  Placement = pos=(4,0,44) rot=(0,0,1;0rad)
  Radius = 1.65
FEATURE [Part::Fuse] Fusion097
  Base = -> Cylinder065
  Tool = -> Cylinder066
FEATURE [Part::Cylinder] Cylinder067  label="Cylinder163"
  Angle = 360
  AttacherType = Attacher::AttachEngine3D
  Height = 43.5
  Placement = pos=(14,0,2) rot=(0,0,1;0rad)
  Radius = 4.8
FEATURE [Part::Cylinder] Cylinder068  label="Cylinder164"
  Angle = 360
  AttacherType = Attacher::AttachEngine3D
  Height = 1.6
  Placement = pos=(14,0,44) rot=(0,0,1;0rad)
  Radius = 1.65
FEATURE [Part::Fuse] Fusion098
  Base = -> Cylinder067
  Tool = -> Cylinder068
FEATURE [Part::Cylinder] Cylinder069  label="Cylinder165"
  Angle = 360
  AttacherType = Attacher::AttachEngine3D
  Height = 43.5
  Placement = pos=(24,0,2) rot=(0,0,1;0rad)
  Radius = 4.8
FEATURE [Part::Cylinder] Cylinder070  label="Cylinder166"
  Angle = 360
  AttacherType = Attacher::AttachEngine3D
  Height = 1.6
  Placement = pos=(24,0,44) rot=(0,0,1;0rad)
  Radius = 1.65
FEATURE [Part::Fuse] Fusion099
  Base = -> Cylinder069
  Tool = -> Cylinder070
FEATURE [Part::Cylinder] Cylinder071  label="Cylinder167"
  Angle = 360
  AttacherType = Attacher::AttachEngine3D
  Height = 43.5
  Placement = pos=(34,0,2) rot=(0,0,1;0rad)
  Radius = 4.8
FEATURE [Part::Cylinder] Cylinder072  label="Cylinder168"
  Angle = 360
  AttacherType = Attacher::AttachEngine3D
  Height = 1.6
  Placement = pos=(34,0,44) rot=(0,0,1;0rad)
  Radius = 1.65
FEATURE [Part::Fuse] Fusion100
  Base = -> Cylinder071
  Tool = -> Cylinder072
FEATURE [Part::Cylinder] Cylinder073  label="Cylinder169"
  Angle = 360
  AttacherType = Attacher::AttachEngine3D
  Height = 43.5
  Placement = pos=(-6,0,2) rot=(0,0,1;0rad)
  Radius = 4.8
FEATURE [Part::Cylinder] Cylinder074  label="Cylinder170"
  Angle = 360
  AttacherType = Attacher::AttachEngine3D
  Height = 1.6
  Placement = pos=(-6,0,44) rot=(0,0,1;0rad)
  Radius = 1.65
FEATURE [Part::Fuse] Fusion101
  Base = -> Cylinder073
  Tool = -> Cylinder074
FEATURE [Part::MultiFuse] Fusion102  label="AAA Batts001"
  Shapes = -> [Fusion101,Fusion097,Fusion098,Fusion099,Fusion100]
FEATURE [Part::Cylinder] Cylinder075  label="Cylinder171"
  Angle = 360
  AttacherType = Attacher::AttachEngine3D
  Height = 10
  Placement = pos=(-9,-20,4) rot=(0,0,1;0rad)
  Radius = 2.75
FEATURE [Part::Cylinder] Cylinder076  label="Cylinder172"
  Angle = 360
  AttacherType = Attacher::AttachEngine3D
  Height = 27
  Placement = pos=(-9,-20,14) rot=(0,0,1;0rad)
  Radius = 2.5
FEATURE [Part::Fuse] Fusion103  label="phototransistor hole"
  Base = -> Cylinder075
  Tool = -> Cylinder076
FEATURE [Part::Cut] Cut045021  label="Phototransistor holder"
  Base = -> Box033
  Tool = -> Fusion103
FEATURE [Part::Fuse] Fusion104  label="Switch Mount with phototransistor hole"
  Base = -> Cut043
  Tool = -> Cut045021
FEATURE [Part::Cut] Cut045022
  Base = -> Box032
  Tool = -> Fusion102
FEATURE [Part::Box] Box034  label="Cube032"
  AttacherType = Attacher::AttachEngine3D
  Height = 2.5
  Length = 55
  Placement = pos=(-13,-9,-1) rot=(0,0,1;0rad)
  Width = 12
FEATURE [Part::Box] Box035  label="Cube033"
  AttacherType = Attacher::AttachEngine3D
  Height = 2.5
  Length = 55
  Placement = pos=(-13,-9,46.5) rot=(0,0,1;0rad)
  Width = 12
FEATURE [Part::Box] Box036  label="Cube034"
  AttacherType = Attacher::AttachEngine3D
  Height = 50
  Length = 2.5
  Placement = pos=(-13,-9,-1) rot=(0,0,1;0rad)
  Width = 12
FEATURE [Part::Box] Box037  label="Cube035"
  AttacherType = Attacher::AttachEngine3D
  Height = 50
  Length = 2.5
  Placement = pos=(39.5,-9,-1) rot=(0,0,1;0rad)
  Width = 12
FEATURE [Part::MultiFuse] Fusion105
  Shapes = -> [Box034,Box036,Box037,Box035]
FEATURE [Part::Box] Box038  label="Cube036"
  AttacherType = Attacher::AttachEngine3D
  Height = 5
  Length = 2
  Placement = pos=(-10.5,-9,46) rot=(0,0,1;0rad)
  Width = 12
FEATURE [Part::Box] Box039  label="Cube037"
  AttacherType = Attacher::AttachEngine3D
  Height = 5
  Length = 2
  Placement = pos=(-10.5,-9,-2) rot=(0,0,1;0rad)
  Width = 12
FEATURE [Part::MultiFuse] Fusion106
  Shapes = -> [Box039,Box038,Box028,Box007]
FEATURE [Part::MultiFuse] Fusion107
  Shapes = -> [Box003,Box004,Box005,Box008]
FEATURE [Part::Cut] Cut045023
  Base = -> Fusion105
  Tool = -> Fusion106
FEATURE [Part::Cut] Cut045024
  Base = -> Cut045023
  Tool = -> Fusion107
FEATURE [Part::Box] Box040  label="Cube038"
  AttacherType = Attacher::AttachEngine3D
  Height = 1.6
  Length = 30
  Placement = pos=(-56,-15.5,-6) rot=(0,0,1;0rad)
  Width = 15
FEATURE [Part::Box] Box041  label="Cube039"
  AttacherType = Attacher::AttachEngine3D
  Height = 10
  Length = 14
  Placement = pos=(-56,-10.5,-4.5) rot=(0,0,1;0rad)
  Width = 6
FEATURE [Part::Box] Box042  label="Cube040"
  AttacherType = Attacher::AttachEngine3D
  Height = 10
  Length = 5.3
  Placement = pos=(-51.7,-11.5,-4.5) rot=(0,0,1;0rad)
  Width = 8
FEATURE [Part::Cut] Cut045025
  Base = -> Box041
  Tool = -> Box042
FEATURE [Part::Fuse] Fusion108  label="Spoke Sensor PCB"
  Base = -> Box040
  Tool = -> Cut045025
FEATURE [Part::Cylinder] Cylinder077  label="Cylinder173"
  Angle = 360
  AttacherType = Attacher::AttachEngine3D
  Height = 14.5
  Placement = pos=(-43.6,-2.4,-9) rot=(0,0,1;0rad)
  Radius = 0.8
FEATURE [Part::Cylinder] Cylinder078  label="Cylinder174"
  Angle = 360
  AttacherType = Attacher::AttachEngine3D
  Height = 14.5
  Placement = pos=(-43.6,-13.8,-9) rot=(0,0,1;0rad)
  Radius = 0.8
FEATURE [Part::Fuse] Fusion109
  Base = -> Cylinder077
  Tool = -> Cylinder078
FEATURE [Part::Cut] Cut045026  label="Spoke Sensor PCB001"
  Base = -> Fusion108
  Tool = -> Fusion109
FEATURE [Part::Cylinder] Cylinder079  label="Cylinder175"
  Angle = 360
  AttacherType = Attacher::AttachEngine3D
  Height = 14.5
  Placement = pos=(-43.6,-2.4,-18) rot=(0,0,1;0rad)
  Radius = 0.8
FEATURE [Part::Cylinder] Cylinder080  label="Cylinder176"
  Angle = 360
  AttacherType = Attacher::AttachEngine3D
  Height = 14.5
  Placement = pos=(-43.6,-13.8,-18) rot=(0,0,1;0rad)
  Radius = 0.8
FEATURE [Part::Fuse] Fusion110  label="Batt Holder"
  Base = -> Cut045022
  Tool = -> Cut045024
FEATURE [Part::Box] Box043  label="Cube041"
  AttacherType = Attacher::AttachEngine3D
  Height = 4
  Length = 12
  Placement = pos=(-50,-16.75,-17) rot=(0,0,1;0rad)
  Width = 23.75
FEATURE [Part::Cone] Cone
  Angle = 360
  AttacherType = Attacher::AttachEngine3D
  Height = 1.5
  Placement = pos=(-43.6,-2.4,-13) rot=(0,0,1;0rad)
  Radius1 = 2.75
  Radius2 = 1.25
FEATURE [Part::Cone] Cone001
  Angle = 360
  AttacherType = Attacher::AttachEngine3D
  Height = 1.5
  Placement = pos=(-43.6,-13.8,-13) rot=(0,0,1;0rad)
  Radius1 = 2.75
  Radius2 = 1.25
FEATURE [Part::Fuse] Fusion111
  Base = -> Cone
  Tool = -> Cone001
FEATURE [Part::Fuse] Fusion113
  Base = -> Cylinder079
  Tool = -> Cylinder080
FEATURE [Part::Cylinder] Cylinder081  label="Cylinder177"
  Angle = 360
  AttacherType = Attacher::AttachEngine3D
  Height = 14.5
  Placement = pos=(-43.6,-2.4,-18) rot=(0,0,1;0rad)
  Radius = 0.8
FEATURE [Part::Cylinder] Cylinder082  label="Cylinder178"
  Angle = 360
  AttacherType = Attacher::AttachEngine3D
  Height = 14.5
  Placement = pos=(-43.6,-13.8,-18) rot=(0,0,1;0rad)
  Radius = 0.8
FEATURE [Part::Box] Box044  label="Cube042"
  AttacherType = Attacher::AttachEngine3D
  Height = 4
  Length = 12
  Placement = pos=(-50,-16.75,-17) rot=(0,0,1;0rad)
  Width = 26.75
FEATURE [Part::Chamfer] Chamfer001
  Base = -> Box044
  Edges = 1 edges r=7: [Edge3]
FEATURE [Part::Cone] Cone002
  Angle = 360
  AttacherType = Attacher::AttachEngine3D
  Height = 1.5
  Placement = pos=(-43.6,-2.4,-13) rot=(0,0,1;0rad)
  Radius1 = 2.75
  Radius2 = 1.25
FEATURE [Part::Cone] Cone003
  Angle = 360
  AttacherType = Attacher::AttachEngine3D
  Height = 1.5
  Placement = pos=(-43.6,-13.8,-13) rot=(0,0,1;0rad)
  Radius1 = 2.75
  Radius2 = 1.25
FEATURE [Part::Fuse] Fusion114
  Base = -> Cone002
  Tool = -> Cone003
FEATURE [Part::Fuse] Fusion115
  Base = -> Chamfer001
  Tool = -> Fusion114
FEATURE [Part::Fuse] Fusion116
  Base = -> Cylinder081
  Tool = -> Cylinder082
FEATURE [Part::Cut] Cut045028
  Base = -> Fusion115
  Tool = -> Fusion116
FEATURE [Part::Mirroring] Part__Mirroring005  label="Cut045028 (Mirror #6)"
  Base = (0,0,0)
  Normal = (1,0,0)
  Placement = pos=(27,0,0) rot=(0,0,1;0rad)
  Source = -> Cut045028
FEATURE [Part::Box] Box045  label="Cube043"
  AttacherType = Attacher::AttachEngine3D
  Height = 5
  Length = 2
  Placement = pos=(28,-9,-2) rot=(0,0,1;0rad)
  Width = 12
FEATURE [Part::Box] Box046  label="Cube044"
  AttacherType = Attacher::AttachEngine3D
  Height = 5
  Length = 2
  Placement = pos=(18.5,-9,46) rot=(0,0,1;0rad)
  Width = 12
FEATURE [Part::Box] Box047  label="Cube045"
  AttacherType = Attacher::AttachEngine3D
  Height = 5
  Length = 2
  Placement = pos=(-2,-9,46) rot=(0,0,1;0rad)
  Width = 12
FEATURE [Part::Box] Box048  label="Cube046"
  AttacherType = Attacher::AttachEngine3D
  Height = 5
  Length = 2
  Placement = pos=(37.5,-9,46) rot=(0,0,1;0rad)
  Width = 12
FEATURE [Part::Box] Box049  label="Cube047"
  AttacherType = Attacher::AttachEngine3D
  Height = 5
  Length = 2
  Placement = pos=(8,-9,-2) rot=(0,0,1;0rad)
  Width = 12
FEATURE [Part::Box] Box050  label="Motor Mount Left001"
  AttacherType = Attacher::AttachEngine3D
  Height = 16
  Length = 4
  Placement = pos=(69,-13,7) rot=(0,0,1;0rad)
  Width = 20
FEATURE [Part::Box] Box051  label="Motor Mount Right001"
  AttacherType = Attacher::AttachEngine3D
  Height = 16
  Length = 4
  Placement = pos=(-46,-13,7) rot=(0,0,1;0rad)
  Width = 20
FEATURE [Part::Box] Box052  label="Motor Support Right001"
  AttacherType = Attacher::AttachEngine3D
  Height = 16
  Length = 10
  Placement = pos=(-25,-1,7) rot=(0,0,1;0rad)
  Width = 8
FEATURE [Part::Box] Box053  label="Motor Support Left001"
  AttacherType = Attacher::AttachEngine3D
  Height = 16
  Length = 10
  Placement = pos=(43,-1,7) rot=(0,0,1;0rad)
  Width = 8
FEATURE [Part::Box] Box054  label="Cube014 Arduino Support cube001"
  AttacherType = Attacher::AttachEngine3D
  Height = 67
  Length = 55
  Placement = pos=(-13,5,-68) rot=(0,0,1;0rad)
  Width = 5
FEATURE [Part::Box] Box055  label="Cube048"
  AttacherType = Attacher::AttachEngine3D
  Height = 117
  Length = 33
  Placement = pos=(-46,7,-68) rot=(0,0,1;0rad)
  Width = 3
FEATURE [Part::Box] Box056  label="Cube049"
  AttacherType = Attacher::AttachEngine3D
  Height = 117
  Length = 31
  Placement = pos=(42,7,-68) rot=(0,0,1;0rad)
  Width = 3
FEATURE [Part::Cylinder] Cylinder083  label="Cylinder179"
  Angle = 360
  AttacherType = Attacher::AttachEngine3D
  Height = 28
  Placement = pos=(48,20,-10) rot=(1,0,0;1.5708rad)
  Radius = 1.6
FEATURE [Part::Cylinder] Cylinder084  label="Cylinder180"
  Angle = 360
  AttacherType = Attacher::AttachEngine3D
  Height = 28
  Placement = pos=(48,20,-17) rot=(1,0,0;1.5708rad)
  Radius = 1.6
FEATURE [Part::Cylinder] Cylinder085  label="Cylinder181"
  Angle = 360
  AttacherType = Attacher::AttachEngine3D
  Height = 28
  Placement = pos=(55,20,-17) rot=(1,0,0;1.5708rad)
  Radius = 1.6
FEATURE [Part::Cylinder] Cylinder086  label="Cylinder182"
  Angle = 360
  AttacherType = Attacher::AttachEngine3D
  Height = 28
  Placement = pos=(55,20,-10) rot=(1,0,0;1.5708rad)
  Radius = 1.6
FEATURE [Part::MultiFuse] Fusion117  label="Mount holes top left001"
  Placement = pos=(-1,0,46) rot=(0,0,1;0rad)
  Shapes = -> [Cylinder084,Cylinder085,Cylinder086,Cylinder083]
FEATURE [Part::MultiFuse] Fusion118  label="Mount holes top right001"
  Placement = pos=(-71,0,46) rot=(0,0,1;0rad)
  Shapes = -> [Cylinder084,Cylinder085,Cylinder086,Cylinder083]
FEATURE [Part::Cylinder] Cylinder087  label="Cylinder183"
  Angle = 360
  AttacherType = Attacher::AttachEngine3D
  Height = 10
  Placement = pos=(0,18,29) rot=(0,0,1;0rad)
  Radius = 2.25
FEATURE [Part::Cylinder] Cylinder088  label="Cylinder184"
  Angle = 360
  AttacherType = Attacher::AttachEngine3D
  Height = 10
  Placement = pos=(4.5,18,32) rot=(0,0,1;0rad)
  Radius = 1
FEATURE [Part::Cylinder] Cylinder089  label="Cylinder185"
  Angle = 360
  AttacherType = Attacher::AttachEngine3D
  Height = 10
  Placement = pos=(-4.5,18,32) rot=(0,0,1;0rad)
  Radius = 1
FEATURE [Part::Fuse] Fusion119  label="Mounting Screw Holes002"
  Base = -> Cylinder088
  Tool = -> Cylinder089
FEATURE [Part::Fuse] Fusion120  label="Motor Holes Left001"
  Base = -> Cylinder087
  Placement = pos=(37,-7,-3) rot=(0.57735,0.57735,0.57735;2.0944rad)
  Tool = -> Fusion119
FEATURE [Part::Cylinder] Cylinder090  label="Cylinder186"
  Angle = 360
  AttacherType = Attacher::AttachEngine3D
  Height = 10
  Placement = pos=(0,18,29) rot=(0,0,1;0rad)
  Radius = 2.25
FEATURE [Part::Cylinder] Cylinder091  label="Cylinder187"
  Angle = 360
  AttacherType = Attacher::AttachEngine3D
  Height = 10
  Placement = pos=(4.5,18,32) rot=(0,0,1;0rad)
  Radius = 1
FEATURE [Part::Cylinder] Cylinder092  label="Cylinder188"
  Angle = 360
  AttacherType = Attacher::AttachEngine3D
  Height = 10
  Placement = pos=(-4.5,18,32) rot=(0,0,1;0rad)
  Radius = 1
FEATURE [Part::Fuse] Fusion121  label="Mounting Screw Holes003"
  Base = -> Cylinder091
  Tool = -> Cylinder092
FEATURE [Part::Fuse] Fusion122  label="Motor Holes Right001"
  Base = -> Cylinder090
  Placement = pos=(-79,-7,-3) rot=(0.57735,0.57735,0.57735;2.0944rad)
  Tool = -> Fusion121
FEATURE [Part::Cylinder] Cylinder093  label="Cylinder189"
  Angle = 360
  AttacherType = Attacher::AttachEngine3D
  Height = 28
  Placement = pos=(40.7,0,-10.3) rot=(1,0,0;1.5708rad)
  Radius = 1.6
FEATURE [Part::Cylinder] Cylinder094  label="Cylinder190"
  Angle = 360
  AttacherType = Attacher::AttachEngine3D
  Height = 28
  Placement = pos=(-2.4,0,-59.8) rot=(1,0,0;1.5708rad)
  Radius = 1.6
FEATURE [Part::Cylinder] Cylinder095  label="Cylinder191"
  Angle = 360
  AttacherType = Attacher::AttachEngine3D
  Height = 28
  Placement = pos=(-5,0,-9) rot=(1,0,0;1.5708rad)
  Radius = 1.6
FEATURE [Part::Cylinder] Cylinder096  label="Cylinder192"
  Angle = 360
  AttacherType = Attacher::AttachEngine3D
  Height = 28
  Placement = pos=(25.5,0,-59.8) rot=(1,0,0;1.5708rad)
  Radius = 1.6
FEATURE [Part::Fuse] Fusion123
  Base = -> Cylinder094
  Tool = -> Cylinder095
FEATURE [Part::Fuse] Fusion124
  Base = -> Cylinder093
  Tool = -> Cylinder096
FEATURE [Part::Fuse] Fusion125  label="Screw holes on Arduino Duo002"
  Base = -> Fusion123
  Tool = -> Fusion124
FEATURE [Part::Mirroring] Part__Mirroring006  label="Screw holes on Arduino Duo (Mirror #1)002"
  Base = (0,0,0)
  Normal = (0,0,1)
  Placement = pos=(-4,10,-67) rot=(0,0,1;0rad)
  Source = -> Fusion125
FEATURE [Part::Mirroring] Part__Mirroring007  label="Screw holes on Arduino Duo (Mirror #1)001 (Mirror #4)001"
  Base = (0,0,0)
  Normal = (1,0,0)
  Placement = pos=(27,0,-6) rot=(0,0,1;0rad)
  Source = -> Part__Mirroring006
FEATURE [Part::Box] Box057  label="Cube050"
  AttacherType = Attacher::AttachEngine3D
  Height = 50
  Length = 47
  Placement = pos=(-9,-8,0) rot=(0,0,1;0rad)
  Width = 12
FEATURE [Part::Box] Box058  label="Cube051"
  AttacherType = Attacher::AttachEngine3D
  Height = 55
  Length = 53
  Placement = pos=(-12,-8,-2.5) rot=(0,0,1;0rad)
  Width = 11
FEATURE [Part::Cut] Cut045029
  Base = -> Box058
  Tool = -> Box057
FEATURE [Part::Box] Box059  label="Cube052"
  AttacherType = Attacher::AttachEngine3D
  Height = 5
  Length = 3
  Placement = pos=(35,-9,-4) rot=(0,0,1;0rad)
  Width = 12
FEATURE [Part::Cut] Cut045030
  Base = -> Cut045029
  Placement = pos=(-9,10,-58) rot=(1,0,0;1.5708rad)
  Tool = -> Box059
FEATURE [Part::Cut] Cut045031
  Base = -> Cut045029
  Placement = pos=(36.7,10,-56.7) rot=(1,0,0;1.5708rad)
  Tool = -> Box059
FEATURE [Part::Cut] Cut045032
  Base = -> Cut045029
  Placement = pos=(-6.4,10,-7.2) rot=(1,0,0;1.5708rad)
  Tool = -> Box059
FEATURE [Part::Cut] Cut045033
  Base = -> Cut045029
  Placement = pos=(21.5,10,-7.2) rot=(1,0,0;1.5708rad)
  Tool = -> Box059
FEATURE [Part::MultiFuse] Fusion126
  Shapes = -> [Cut045030,Cut045033,Cut045031,Cut045032]
FEATURE [Part::Mirroring] Part__Mirroring008  label="Hex Holes001"
  Base = (0,0,0)
  Normal = (1,0,0)
  Placement = pos=(27,0,-6) rot=(0,0,1;0rad)
  Source = -> Fusion126
FEATURE [Part::Box] Box060  label="Cube053"
  AttacherType = Attacher::AttachEngine3D
  Height = 5
  Length = 2
  Placement = pos=(37.5,-9,-2) rot=(0,0,1;0rad)
  Width = 12
FEATURE [Part::Box] Box061  label="Battery Base001"
  AttacherType = Attacher::AttachEngine3D
  Height = 50
  Length = 55
  Placement = pos=(-13,3,-1) rot=(0,0,1;0rad)
  Width = 7
FEATURE [Part::Cylinder] Cylinder097  label="Cylinder193"
  Angle = 360
  AttacherType = Attacher::AttachEngine3D
  Height = 42
  Radius = 4.8
FEATURE [Part::Cylinder] Cylinder098  label="Cylinder194"
  Angle = 360
  AttacherType = Attacher::AttachEngine3D
  Height = 1.6
  Placement = pos=(0,0,42) rot=(0,0,1;0rad)
  Radius = 1.65
FEATURE [Part::Fuse] Fusion127
  Base = -> Cylinder097
  Placement = pos=(2,0,0) rot=(0,0,1;0rad)
  Tool = -> Cylinder098
FEATURE [Part::Cylinder] Cylinder099  label="Cylinder195"
  Angle = 360
  AttacherType = Attacher::AttachEngine3D
  Height = 42
  Radius = 4.8
FEATURE [Part::Cylinder] Cylinder100  label="Cylinder196"
  Angle = 360
  AttacherType = Attacher::AttachEngine3D
  Height = 1.6
  Placement = pos=(0,0,42) rot=(0,0,1;0rad)
  Radius = 1.65
FEATURE [Part::Fuse] Fusion128
  Base = -> Cylinder099
  Placement = pos=(12,0,0) rot=(0,0,1;0rad)
  Tool = -> Cylinder100
FEATURE [Part::Cylinder] Cylinder101  label="Cylinder197"
  Angle = 360
  AttacherType = Attacher::AttachEngine3D
  Height = 42
  Radius = 4.8
FEATURE [Part::Cylinder] Cylinder102  label="Cylinder198"
  Angle = 360
  AttacherType = Attacher::AttachEngine3D
  Height = 1.6
  Placement = pos=(0,0,42) rot=(0,0,1;0rad)
  Radius = 1.65
FEATURE [Part::Fuse] Fusion129
  Base = -> Cylinder101
  Placement = pos=(22,0,0) rot=(0,0,1;0rad)
  Tool = -> Cylinder102
FEATURE [Part::Cylinder] Cylinder103  label="Cylinder199"
  Angle = 360
  AttacherType = Attacher::AttachEngine3D
  Height = 42
  Radius = 4.8
FEATURE [Part::Cylinder] Cylinder104  label="Cylinder200"
  Angle = 360
  AttacherType = Attacher::AttachEngine3D
  Height = 1.6
  Placement = pos=(0,0,42) rot=(0,0,1;0rad)
  Radius = 1.65
FEATURE [Part::Fuse] Fusion130
  Base = -> Cylinder103
  Placement = pos=(32,0,0) rot=(0,0,1;0rad)
  Tool = -> Cylinder104
FEATURE [Part::Cylinder] Cylinder105  label="Cylinder201"
  Angle = 360
  AttacherType = Attacher::AttachEngine3D
  Height = 42
  Radius = 4.8
FEATURE [Part::Cylinder] Cylinder106  label="Cylinder202"
  Angle = 360
  AttacherType = Attacher::AttachEngine3D
  Height = 1.6
  Placement = pos=(0,0,42) rot=(0,0,1;0rad)
  Radius = 1.65
FEATURE [Part::Fuse] Fusion131
  Base = -> Cylinder105
  Placement = pos=(-8,0,0) rot=(0,0,1;0rad)
  Tool = -> Cylinder106
FEATURE [Part::MultiFuse] Fusion132  label="AAA Batts002"
  Placement = pos=(2,0,2) rot=(0,0,1;0rad)
  Shapes = -> [Fusion131,Fusion127,Fusion128,Fusion129,Fusion130]
FEATURE [Part::Cut] Cut045034
  Base = -> Box061
  Tool = -> Fusion132
FEATURE [Part::Box] Box062  label="Cube054"
  AttacherType = Attacher::AttachEngine3D
  Height = 2.5
  Length = 55
  Placement = pos=(-13,-9,-1) rot=(0,0,1;0rad)
  Width = 12
FEATURE [Part::Box] Box063  label="Cube055"
  AttacherType = Attacher::AttachEngine3D
  Height = 2.5
  Length = 55
  Placement = pos=(-13,-9,46.5) rot=(0,0,1;0rad)
  Width = 12
FEATURE [Part::Box] Box064  label="Cube056"
  AttacherType = Attacher::AttachEngine3D
  Height = 50
  Length = 2.5
  Placement = pos=(-13,-9,-1) rot=(0,0,1;0rad)
  Width = 12
FEATURE [Part::Box] Box065  label="Cube057"
  AttacherType = Attacher::AttachEngine3D
  Height = 50
  Length = 2.5
  Placement = pos=(39.5,-9,-1) rot=(0,0,1;0rad)
  Width = 12
FEATURE [Part::MultiFuse] Fusion133
  Shapes = -> [Box062,Box064,Box065,Box063]
FEATURE [Part::Box] Box066  label="Cube058"
  AttacherType = Attacher::AttachEngine3D
  Height = 5
  Length = 2
  Placement = pos=(-10.5,-9,46) rot=(0,0,1;0rad)
  Width = 12
FEATURE [Part::Box] Box067  label="Cube059"
  AttacherType = Attacher::AttachEngine3D
  Height = 5
  Length = 2
  Placement = pos=(-10.5,-9,-2) rot=(0,0,1;0rad)
  Width = 12
FEATURE [Part::MultiFuse] Fusion134
  Shapes = -> [Box067,Box066,Box060,Box048]
FEATURE [Part::MultiFuse] Fusion135
  Shapes = -> [Box045,Box046,Box047,Box049]
FEATURE [Part::Cut] Cut045035
  Base = -> Fusion133
  Tool = -> Fusion134
FEATURE [Part::Cut] Cut045036
  Base = -> Cut045035
  Tool = -> Fusion135
FEATURE [Part::Cylinder] Cylinder107  label="Cylinder203"
  Angle = 360
  AttacherType = Attacher::AttachEngine3D
  Height = 14.5
  Placement = pos=(-43.6,-2.4,-15) rot=(0,0,1;0rad)
  Radius = 0.8
FEATURE [Part::Cylinder] Cylinder108  label="Cylinder204"
  Angle = 360
  AttacherType = Attacher::AttachEngine3D
  Height = 14.5
  Placement = pos=(-43.6,-13.8,-15) rot=(0,0,1;0rad)
  Radius = 0.8
FEATURE [Part::Fuse] Fusion136
  Base = -> Cut045034
  Tool = -> Cut045036
FEATURE [Part::Box] Box068  label="Cube060"
  AttacherType = Attacher::AttachEngine3D
  Height = 4
  Length = 12
  Placement = pos=(-50,-16.75,-14) rot=(0,0,1;0rad)
  Width = 26.75
FEATURE [Part::Chamfer] Chamfer002
  Base = -> Box068
  Edges = 1 edges r=7: [Edge3]
FEATURE [Part::Cone] Cone004
  Angle = 360
  AttacherType = Attacher::AttachEngine3D
  Height = 1.5
  Placement = pos=(-43.6,-2.4,-10) rot=(0,0,1;0rad)
  Radius1 = 2.75
  Radius2 = 1.25
FEATURE [Part::Cone] Cone005
  Angle = 360
  AttacherType = Attacher::AttachEngine3D
  Height = 1.5
  Placement = pos=(-43.6,-13.8,-10) rot=(0,0,1;0rad)
  Radius1 = 2.75
  Radius2 = 1.25
FEATURE [Part::Fuse] Fusion137
  Base = -> Cone004
  Tool = -> Cone005
FEATURE [Part::Fuse] Fusion138
  Base = -> Chamfer002
  Tool = -> Fusion137
FEATURE [Part::Fuse] Fusion139
  Base = -> Cylinder107
  Tool = -> Cylinder108
FEATURE [Part::Cut] Cut045037
  Base = -> Fusion138
  Tool = -> Fusion139
FEATURE [Part::Cylinder] Cylinder109  label="Cylinder205"
  Angle = 360
  AttacherType = Attacher::AttachEngine3D
  Height = 14.5
  Placement = pos=(-43.6,-2.4,-15) rot=(0,0,1;0rad)
  Radius = 0.8
FEATURE [Part::Cylinder] Cylinder110  label="Cylinder206"
  Angle = 360
  AttacherType = Attacher::AttachEngine3D
  Height = 14.5
  Placement = pos=(-43.6,-13.8,-15) rot=(0,0,1;0rad)
  Radius = 0.8
FEATURE [Part::Box] Box069  label="Cube061"
  AttacherType = Attacher::AttachEngine3D
  Height = 4
  Length = 12
  Placement = pos=(-50,-16.75,-14) rot=(0,0,1;0rad)
  Width = 26.75
FEATURE [Part::Chamfer] Chamfer003
  Base = -> Box069
  Edges = 1 edges r=7: [Edge3]
FEATURE [Part::Cone] Cone006
  Angle = 360
  AttacherType = Attacher::AttachEngine3D
  Height = 1.5
  Placement = pos=(-43.6,-2.4,-10) rot=(0,0,1;0rad)
  Radius1 = 2.75
  Radius2 = 1.25
FEATURE [Part::Cone] Cone007
  Angle = 360
  AttacherType = Attacher::AttachEngine3D
  Height = 1.5
  Placement = pos=(-43.6,-13.8,-10) rot=(0,0,1;0rad)
  Radius1 = 2.75
  Radius2 = 1.25
FEATURE [Part::Fuse] Fusion140
  Base = -> Cone006
  Tool = -> Cone007
FEATURE [Part::Fuse] Fusion141
  Base = -> Chamfer003
  Tool = -> Fusion140
FEATURE [Part::Fuse] Fusion142
  Base = -> Cylinder109
  Tool = -> Cylinder110
FEATURE [Part::Cut] Cut045038
  Base = -> Fusion141
  Tool = -> Fusion142
FEATURE [Part::Mirroring] Part__Mirroring009  label="Cut045028 (Mirror #6)001"
  Base = (0,0,0)
  Normal = (1,0,0)
  Placement = pos=(27,0,0) rot=(0,0,1;0rad)
  Source = -> Cut045038
FEATURE [Part::Cut] Cut045039
  Base = -> Box050
  Tool = -> Fusion120
FEATURE [Part::Cut] Cut045040
  Base = -> Box051
  Tool = -> Fusion122
FEATURE [Part::MultiFuse] Fusion143
  Shapes = -> [Box054,Box055,Box056]
FEATURE [Part::Fuse] Fusion144
  Base = -> Fusion136
  Tool = -> Fusion143
FEATURE [Part::MultiFuse] Fusion145
  Shapes = -> [Fusion144,Cut045040,Cut045039]
FEATURE [Part::MultiFuse] Fusion146
  Shapes = -> [Fusion145,Part__Mirroring009,Cut045037]
FEATURE [Part::Cut] Cut045041
  Base = -> Fusion146
  Tool = -> Fusion117
FEATURE [Part::Cut] Cut045042
  Base = -> Cut045041
  Tool = -> Fusion118
FEATURE [Part::Cut] Cut045043
  Base = -> Cut045042
  Tool = -> Part__Mirroring007
FEATURE [Part::Cut] Cut045044
  Base = -> Cut045043
  Tool = -> Part__Mirroring008
FEATURE [Part::MultiFuse] Fusion147
  Shapes = -> [Cut045044,Box053,Box052]
FEATURE [Part::Chamfer] Chamfer004
  Base = -> Fusion147
  Edges = 1 edges r=25: [Edge43]
FEATURE [Part::Chamfer] Chamfer005
  Base = -> Chamfer004
  Edges = 1 edges r=25: [Edge225]
FEATURE [Part::Chamfer] Chamfer006
  Base = -> Chamfer005
  Edges = 1 edges r=30: [Edge58]
FEATURE [Part::Chamfer] Chamfer007
  Base = -> Chamfer006
  Edges = 1 edges r=30: [Edge148]
FEATURE [Part::Fillet] Fillet
  Base = -> Chamfer007
  Edges = 1 edges r=2: [Edge233]
FEATURE [Part::Fillet] Fillet001
  Base = -> Fillet
  Edges = 1 edges r=2: [Edge6]
FEATURE [Part::Fillet] Fillet002
  Base = -> Fillet001
  Edges = 1 edges r=2: [Edge2]
FEATURE [Part::Fillet] Fillet003
  Base = -> Fillet002
  Edges = 1 edges r=2: [Edge357]
FEATURE [Part::Fillet] Fillet004
  Base = -> Fillet003
  Edges = 1 edges r=2: [Edge6]
FEATURE [Part::Fillet] Fillet005
  Base = -> Fillet004
  Edges = 1 edges r=2: [Edge2]
FEATURE [Part::Fillet] Fillet006
  Base = -> Fillet005
  Edges = 1 edges r=2: [Edge407]
FEATURE [Part::Fillet] Fillet007
  Base = -> Fillet006
  Edges = 1 edges r=2: [Edge2]
FEATURE [Part::Fillet] Fillet008
  Base = -> Fillet007
  Edges = 1 edges r=2: [Edge369]
FEATURE [Part::Fillet] Fillet009
  Base = -> Fillet008
  Edges = 1 edges r=2: [Edge2]
FEATURE [Part::Cylinder] Cylinder111  label="Cylinder207"
  Angle = 360
  AttacherType = Attacher::AttachEngine3D
  Height = 28
  Placement = pos=(45,6,47) rot=(0.707107,0,0.707107;4.01426rad)
  Radius = 0.5
FEATURE [Part::Cylinder] Cylinder112  label="Cylinder208"
  Angle = 360
  AttacherType = Attacher::AttachEngine3D
  Height = 28
  Placement = pos=(66,6,26) rot=(0.707107,0,0.707107;4.01426rad)
  Radius = 0.5
FEATURE [Part::Cut] Cut045045
  Base = -> Fillet009
  Tool = -> Cylinder111
FEATURE [Part::Cut] Cut045046
  Base = -> Cut045045
  Tool = -> Cylinder112
FEATURE [Part::Cylinder] Cylinder113  label="Cylinder209"
  Angle = 360
  AttacherType = Attacher::AttachEngine3D
  Height = 28
  Placement = pos=(66,6,26) rot=(0.707107,0,0.707107;4.01426rad)
  Radius = 0.5
FEATURE [Part::Mirroring] Part__Mirroring010  label="Cylinder137 (Mirror #7)"
  Base = (0,0,0)
  Normal = (1,0,0)
  Placement = pos=(27,0,0) rot=(0,0,1;0rad)
  Source = -> Cylinder113
FEATURE [Part::Cylinder] Cylinder114  label="Cylinder210"
  Angle = 360
  AttacherType = Attacher::AttachEngine3D
  Height = 28
  Placement = pos=(45,6,47) rot=(0.707107,0,0.707107;4.01426rad)
  Radius = 0.5
FEATURE [Part::Mirroring] Part__Mirroring011  label="Cylinder138 (Mirror #8)"
  Base = (0,0,0)
  Normal = (1,0,0)
  Placement = pos=(27,0,0) rot=(0,0,1;0rad)
  Source = -> Cylinder114
FEATURE [Part::Cut] Cut045047
  Base = -> Cut045046
  Tool = -> Part__Mirroring010
FEATURE [Part::Cut] Cut045048  label="Old Layout"
  Base = -> Cut045047
  Tool = -> Part__Mirroring011
FEATURE [Part::Cylinder] Cylinder115  label="Arduino Cylinder191"
  Angle = 360
  AttacherType = Attacher::AttachEngine3D
  Height = 28
  Placement = pos=(4,11,-8.6) rot=(1,0,0;1.5708rad)
  Radius = 1.6
FEATURE [Part::Cylinder] Cylinder116  label="Arduino Cylinder192"
  Angle = 360
  AttacherType = Attacher::AttachEngine3D
  Height = 28
  Placement = pos=(31.9,11,-8.6) rot=(1,0,0;1.5708rad)
  Radius = 1.6
FEATURE [Part::Cylinder] Cylinder117  label="Arduino Cylinder193"
  Angle = 360
  AttacherType = Attacher::AttachEngine3D
  Height = 28
  Placement = pos=(-11.2,11,-59.4) rot=(1,0,0;1.5708rad)
  Radius = 1.6
FEATURE [Part::Cylinder] Cylinder118  label="Arduino Cylinder194"
  Angle = 360
  AttacherType = Attacher::AttachEngine3D
  Height = 28
  Placement = pos=(37.2,11,-60.5) rot=(1,0,0;1.5708rad)
  Radius = 1.6
FEATURE [Part::Cylinder] Cylinder119  label="Arduino Cylinder195"
  Angle = 360
  AttacherType = Attacher::AttachEngine3D
  Height = 2.5
  Placement = pos=(4,13,-8.6) rot=(1,0,0;1.5708rad)
  Radius = 4
FEATURE [Part::Feature] Box014001
  Placement = pos=(3.88157,4,-2.89487) rot=(0,1,0;1.0472rad)
  shape: bbox 13.66 x 10 x 13.66 mm, 6 faces (baked)
FEATURE [Part::Feature] Box014002
  Placement = pos=(8.88157,4,-5.64487) rot=(0,1,0;2.0944rad)
  shape: bbox 13.66 x 10 x 13.66 mm, 6 faces (baked)
FEATURE [Part::Feature] Box014003
  Placement = pos=(9,4,-11.35) rot=(0,1,0;3.14159rad)
  shape: bbox 10 x 10 x 10 mm, 6 faces (baked)
FEATURE [Part::Feature] Box014004
  Placement = pos=(4.11843,4,-14.3051) rot=(0,1,0;4.18879rad)
  shape: bbox 13.66 x 10 x 13.66 mm, 6 faces (baked)
FEATURE [Part::Feature] Box014005
  Placement = pos=(-0.88157,4,-11.5551) rot=(0,-1,0;1.0472rad)
  shape: bbox 13.66 x 10 x 13.66 mm, 6 faces (baked)
FEATURE [Part::MultiFuse] Fusion148
  Shapes = -> [Box014001,Box014002,Box014004,Box014003,Box014005,Box014]
FEATURE [Part::Cut] Cut045049  label="M3 Nut004"
  Base = -> Cylinder119
  Placement = pos=(0,-3,0) rot=(0,0,1;0rad)
  Tool = -> Fusion148
FEATURE [Part::Box] Box014006  label="Not used Cube001"
  AttacherType = Attacher::AttachEngine3D
  Height = 10
  Length = 10
  Placement = pos=(-1,4,-5.85) rot=(0,0,1;0rad)
  Width = 10
FEATURE [Part::Cylinder] Cylinder120  label="Arduino Cylinder196"
  Angle = 360
  AttacherType = Attacher::AttachEngine3D
  Height = 2.5
  Placement = pos=(4,13,-8.6) rot=(1,0,0;1.5708rad)
  Radius = 4
FEATURE [Part::Feature] Box014007
  Placement = pos=(3.88157,4,-2.89487) rot=(0,1,0;1.0472rad)
  shape: bbox 13.66 x 10 x 13.66 mm, 6 faces (baked)
FEATURE [Part::Feature] Box014008
  Placement = pos=(8.88157,4,-5.64487) rot=(0,1,0;2.0944rad)
  shape: bbox 13.66 x 10 x 13.66 mm, 6 faces (baked)
FEATURE [Part::Feature] Box014009
  Placement = pos=(9,4,-11.35) rot=(0,1,0;3.14159rad)
  shape: bbox 10 x 10 x 10 mm, 6 faces (baked)
FEATURE [Part::Feature] Box014010
  Placement = pos=(4.11843,4,-14.3051) rot=(0,1,0;4.18879rad)
  shape: bbox 13.66 x 10 x 13.66 mm, 6 faces (baked)
FEATURE [Part::Feature] Box014011
  Placement = pos=(-0.88157,4,-11.5551) rot=(0,-1,0;1.0472rad)
  shape: bbox 13.66 x 10 x 13.66 mm, 6 faces (baked)
FEATURE [Part::MultiFuse] Fusion149
  Shapes = -> [Box014007,Box014008,Box014010,Box014009,Box014011,Box014006]
FEATURE [Part::Cut] Cut045050  label="M3 Nut005"
  Base = -> Cylinder120
  Placement = pos=(27.9,-3,0) rot=(0,0,1;0rad)
  Tool = -> Fusion149
FEATURE [Part::Box] Box014012  label="Not used Cube002"
  AttacherType = Attacher::AttachEngine3D
  Height = 10
  Length = 10
  Placement = pos=(-1,4,-5.85) rot=(0,0,1;0rad)
  Width = 10
FEATURE [Part::Cylinder] Cylinder121  label="Arduino Cylinder197"
  Angle = 360
  AttacherType = Attacher::AttachEngine3D
  Height = 2.5
  Placement = pos=(4,13,-8.6) rot=(1,0,0;1.5708rad)
  Radius = 4
FEATURE [Part::Feature] Box014013
  Placement = pos=(3.88157,4,-2.89487) rot=(0,1,0;1.0472rad)
  shape: bbox 13.66 x 10 x 13.66 mm, 6 faces (baked)
FEATURE [Part::Feature] Box014014
  Placement = pos=(8.88157,4,-5.64487) rot=(0,1,0;2.0944rad)
  shape: bbox 13.66 x 10 x 13.66 mm, 6 faces (baked)
FEATURE [Part::Feature] Box014015
  Placement = pos=(9,4,-11.35) rot=(0,1,0;3.14159rad)
  shape: bbox 10 x 10 x 10 mm, 6 faces (baked)
FEATURE [Part::Feature] Box014016
  Placement = pos=(4.11843,4,-14.3051) rot=(0,1,0;4.18879rad)
  shape: bbox 13.66 x 10 x 13.66 mm, 6 faces (baked)
FEATURE [Part::Feature] Box014017
  Placement = pos=(-0.88157,4,-11.5551) rot=(0,-1,0;1.0472rad)
  shape: bbox 13.66 x 10 x 13.66 mm, 6 faces (baked)
FEATURE [Part::MultiFuse] Fusion150
  Shapes = -> [Box014013,Box014014,Box014016,Box014015,Box014017,Box014012]
FEATURE [Part::Cut] Cut045051  label="M3 Nut006"
  Base = -> Cylinder121
  Placement = pos=(-15.2,-3,-50.8) rot=(0,0,1;0rad)
  Tool = -> Fusion150
FEATURE [Part::Box] Box014018  label="Not used Cube003"
  AttacherType = Attacher::AttachEngine3D
  Height = 10
  Length = 10
  Placement = pos=(-1,4,-5.85) rot=(0,0,1;0rad)
  Width = 10
FEATURE [Part::Cylinder] Cylinder122  label="Arduino Cylinder198"
  Angle = 360
  AttacherType = Attacher::AttachEngine3D
  Height = 2.5
  Placement = pos=(4,13,-8.6) rot=(1,0,0;1.5708rad)
  Radius = 4
FEATURE [Part::Feature] Box014019
  Placement = pos=(3.88157,4,-2.89487) rot=(0,1,0;1.0472rad)
  shape: bbox 13.66 x 10 x 13.66 mm, 6 faces (baked)
FEATURE [Part::Feature] Box014020
  Placement = pos=(8.88157,4,-5.64487) rot=(0,1,0;2.0944rad)
  shape: bbox 13.66 x 10 x 13.66 mm, 6 faces (baked)
FEATURE [Part::Feature] Box014021
  Placement = pos=(9,4,-11.35) rot=(0,1,0;3.14159rad)
  shape: bbox 10 x 10 x 10 mm, 6 faces (baked)
FEATURE [Part::Feature] Box014022
  Placement = pos=(4.11843,4,-14.3051) rot=(0,1,0;4.18879rad)
  shape: bbox 13.66 x 10 x 13.66 mm, 6 faces (baked)
FEATURE [Part::Feature] Box014023
  Placement = pos=(-0.88157,4,-11.5551) rot=(0,-1,0;1.0472rad)
  shape: bbox 13.66 x 10 x 13.66 mm, 6 faces (baked)
FEATURE [Part::MultiFuse] Fusion151
  Shapes = -> [Box014019,Box014020,Box014022,Box014021,Box014023,Box014018]
FEATURE [Part::Cut] Cut045052  label="M3 Nut007"
  Base = -> Cylinder122
  Placement = pos=(33.2,-3,-51.9) rot=(0,0,1;0rad)
  Tool = -> Fusion151
FEATURE [Part::Box] Box014024  label="Cube062"
  AttacherType = Attacher::AttachEngine3D
  Height = 67
  Length = 65
  Placement = pos=(-16,-13,-6) rot=(0,0,1;0rad)
  Width = 8
FEATURE [Part::Cut] Cut045053  label="BAtt Holder"
  Base = -> Fusion110
  Tool = -> Box014024
FEATURE [Part::Cylinder] Cylinder123  label="Cylinder211"
  Angle = 360
  AttacherType = Attacher::AttachEngine3D
  Height = 28
  Placement = pos=(45,6,47) rot=(0.707107,0,0.707107;4.01426rad)
  Radius = 0.5
FEATURE [Part::Cylinder] Cylinder124  label="Cylinder212"
  Angle = 360
  AttacherType = Attacher::AttachEngine3D
  Height = 28
  Placement = pos=(66,6,26) rot=(0.707107,0,0.707107;4.01426rad)
  Radius = 0.5
FEATURE [Part::Cylinder] Cylinder125  label="Cylinder213"
  Angle = 360
  AttacherType = Attacher::AttachEngine3D
  Height = 28
  Placement = pos=(45,6,47) rot=(0.707107,0,0.707107;4.01426rad)
  Radius = 0.5
FEATURE [Part::Cylinder] Cylinder126  label="Cylinder214"
  Angle = 360
  AttacherType = Attacher::AttachEngine3D
  Height = 28
  Placement = pos=(66,6,26) rot=(0.707107,0,0.707107;4.01426rad)
  Radius = 0.5
FEATURE [Part::Mirroring] Part__Mirroring012  label="Cylinder211 (Mirror #13)"
  Base = (0,0,0)
  Normal = (1,0,0)
  Placement = pos=(27,0,0) rot=(0,0,1;0rad)
  Source = -> Cylinder125
FEATURE [Part::Mirroring] Part__Mirroring013  label="Cylinder212 (Mirror #14)"
  Base = (0,0,0)
  Normal = (1,0,0)
  Placement = pos=(27,0,0) rot=(0,0,1;0rad)
  Source = -> Cylinder126
FEATURE [Part::Chamfer] Chamfer008
  Base = -> Fusion104
  Edges = 1 edges r=0.5: [Edge67]
FEATURE [Part::Chamfer] Chamfer009  label="Switch Mount"
  Base = -> Chamfer008
  Edges = 1 edges r=0.5: [Edge6]
FEATURE [Part::Box] Box014025  label="Cube063"
  AttacherType = Attacher::AttachEngine3D
  Height = 17
  Length = 15
  Placement = pos=(-46,4,-30) rot=(0,0,1;0rad)
  Width = 3
FEATURE [Part::Cylinder] Cylinder127  label="Cylinder215"
  Angle = 360
  AttacherType = Attacher::AttachEngine3D
  Height = 10
  Placement = pos=(-39,9,-22) rot=(1,0,0;1.5708rad)
  Radius = 3
FEATURE [Part::Box] Box014026  label="Cube064"
  AttacherType = Attacher::AttachEngine3D
  Height = 9.5
  Length = 15
  Placement = pos=(-46,0,-27) rot=(0,0,1;0rad)
  Width = 3
FEATURE [Part::Cylinder] Cylinder128  label="Cylinder216"
  Angle = 360
  AttacherType = Attacher::AttachEngine3D
  Height = 14
  Placement = pos=(-39,11,-22) rot=(1,0,0;1.5708rad)
  Radius = 1.5
FEATURE [Part::Cut] Cut045054
  Base = -> Box014025
  Tool = -> Cylinder127
FEATURE [Part::Cylinder] Cylinder129  label="Sensor Mount Hole"
  Angle = 360
  AttacherType = Attacher::AttachEngine3D
  Height = 14
  Placement = pos=(-39,11,-22) rot=(1,0,0;1.5708rad)
  Radius = 1.5
FEATURE [Part::Cut] Cut045055  label="Printed Washer"
  Base = -> Box014026
  Tool = -> Cylinder128
FEATURE [Part::Box] Box014027  label="Cube065"
  AttacherType = Attacher::AttachEngine3D
  Height = 23
  Length = 22
  Placement = pos=(-46,4,0) rot=(0,0,1;0rad)
  Width = 3
FEATURE [Part::Cylinder] Cylinder130  label="Cylinder218"
  Angle = 360
  AttacherType = Attacher::AttachEngine3D
  Height = 14
  Placement = pos=(-38,11,4) rot=(1,0,0;1.5708rad)
  Radius = 1.5
FEATURE [Part::Cylinder] Cylinder131  label="Cylinder219"
  Angle = 360
  AttacherType = Attacher::AttachEngine3D
  Height = 14
  Placement = pos=(-28,11,4) rot=(1,0,0;1.5708rad)
  Radius = 1.5
FEATURE [Part::Cylinder] Cylinder132  label="Cylinder220"
  Angle = 360
  AttacherType = Attacher::AttachEngine3D
  Height = 14.5
  Placement = pos=(-53.76,-13.8,-18) rot=(0,0,1;0rad)
  Radius = 0.8
FEATURE [Part::Box] Box014028  label="Cube066"
  AttacherType = Attacher::AttachEngine3D
  Height = 4
  Length = 19
  Placement = pos=(-57,-16.75,-17) rot=(0,0,1;0rad)
  Width = 8.75
FEATURE [Part::Cone] Cone008
  Angle = 360
  AttacherType = Attacher::AttachEngine3D
  Height = 1.5
  Placement = pos=(-53.76,-13.8,-13) rot=(0,0,1;0rad)
  Radius1 = 2.75
  Radius2 = 1.25
FEATURE [Part::Fuse] Fusion152
  Base = -> Fusion111
  Tool = -> Cone008
FEATURE [Part::Fuse] Fusion153
  Base = -> Fusion113
  Tool = -> Cylinder132
FEATURE [Part::Fuse] Fusion154
  Base = -> Box043
  Tool = -> Box014028
FEATURE [Part::Cylinder] Cylinder133  label="Cylinder221"
  Angle = 360
  AttacherType = Attacher::AttachEngine3D
  Height = 14.5
  Placement = pos=(-43.6,-2.4,-18) rot=(0,0,1;0rad)
  Radius = 0.8
FEATURE [Part::Cylinder] Cylinder134  label="Cylinder222"
  Angle = 360
  AttacherType = Attacher::AttachEngine3D
  Height = 14.5
  Placement = pos=(-43.6,-13.8,-18) rot=(0,0,1;0rad)
  Radius = 0.8
FEATURE [Part::Box] Box014029  label="Cube067"
  AttacherType = Attacher::AttachEngine3D
  Height = 4
  Length = 12
  Placement = pos=(-50,-16.75,-17) rot=(0,0,1;0rad)
  Width = 23.75
FEATURE [Part::Cone] Cone009
  Angle = 360
  AttacherType = Attacher::AttachEngine3D
  Height = 1.5
  Placement = pos=(-43.6,-2.4,-13) rot=(0,0,1;0rad)
  Radius1 = 2.75
  Radius2 = 1.25
FEATURE [Part::Cone] Cone010
  Angle = 360
  AttacherType = Attacher::AttachEngine3D
  Height = 1.5
  Placement = pos=(-43.6,-13.8,-13) rot=(0,0,1;0rad)
  Radius1 = 2.75
  Radius2 = 1.25
FEATURE [Part::Fuse] Fusion157
  Base = -> Cone009
  Tool = -> Cone010
FEATURE [Part::Fuse] Fusion158
  Base = -> Cylinder133
  Tool = -> Cylinder134
FEATURE [Part::Box] Box014030  label="Cube068"
  AttacherType = Attacher::AttachEngine3D
  Height = 14
  Length = 15
  Placement = pos=(-46,4,-27) rot=(0,0,1;0rad)
  Width = 3
FEATURE [Part::Cylinder] Cylinder135  label="Cylinder223"
  Angle = 360
  AttacherType = Attacher::AttachEngine3D
  Height = 10
  Placement = pos=(-39,9,-22) rot=(1,0,0;1.5708rad)
  Radius = 3
FEATURE [Part::Cut] Cut045057
  Base = -> Box014030
  Tool = -> Cylinder135
FEATURE [Part::Cylinder] Cylinder136  label="Cylinder224"
  Angle = 360
  AttacherType = Attacher::AttachEngine3D
  Height = 14.5
  Placement = pos=(-53.76,-13.8,-18) rot=(0,0,1;0rad)
  Radius = 0.8
FEATURE [Part::Box] Box014031  label="Cube069"
  AttacherType = Attacher::AttachEngine3D
  Height = 4
  Length = 19
  Placement = pos=(-57,-16.75,-17) rot=(0,0,1;0rad)
  Width = 8.75
FEATURE [Part::Cone] Cone011
  Angle = 360
  AttacherType = Attacher::AttachEngine3D
  Height = 1.5
  Placement = pos=(-53.76,-13.8,-13) rot=(0,0,1;0rad)
  Radius1 = 2.75
  Radius2 = 1.25
FEATURE [Part::Fuse] Fusion159
  Base = -> Fusion157
  Tool = -> Cone011
FEATURE [Part::Fuse] Fusion160
  Base = -> Fusion158
  Tool = -> Cylinder136
FEATURE [Part::Fuse] Fusion161
  Base = -> Box014029
  Tool = -> Box014031
FEATURE [Part::Fuse] Fusion162
  Base = -> Cut045057
  Tool = -> Fusion161
FEATURE [Part::Fuse] Fusion163
  Base = -> Fusion159
  Tool = -> Fusion162
FEATURE [Part::Cut] Cut045058
  Base = -> Fusion163
  Tool = -> Fusion160
FEATURE [Part::Chamfer] Chamfer010
  Base = -> Cut045058
  Edges = 1 edges r=6.99: [Edge15]
FEATURE [Part::Fillet] Fillet015
  Base = -> Chamfer010
  Edges = 1 edges r=1: [Edge51]
FEATURE [Part::Fillet] Fillet016
  Base = -> Fillet015
  Edges = 1 edges r=1: [Edge11]
FEATURE [Part::Fillet] Fillet017
  Base = -> Fillet016
  Edges = 1 edges r=1: [Edge37]
FEATURE [Part::Fillet] Fillet018
  Base = -> Fillet017
  Edges = 1 edges r=5: [Edge54]
FEATURE [Part::Fillet] Fillet019  label="Sensor Mount001"
  Base = -> Fillet018
  Edges = 1 edges r=5: [Edge12]
FEATURE [Part::Mirroring] Part__Mirroring014  label="Sensor Mount001 (Mirror #15)"
  Base = (0,0,0)
  Normal = (1,0,0)
  Placement = pos=(27,0,0) rot=(0,0,1;0rad)
  Source = -> Fillet019
FEATURE [Part::Fuse] Fusion164
  Base = -> Box011
  Tool = -> Box014027
FEATURE [Part::Cut] Cut045059
  Base = -> Fusion164
  Tool = -> Fusion073
FEATURE [Part::Fuse] Fusion165
  Base = -> Cylinder130
  Tool = -> Cylinder131
FEATURE [Part::Cylinder] Cylinder137  label="Cylinder225"
  Angle = 360
  AttacherType = Attacher::AttachEngine3D
  Height = 14
  Placement = pos=(-38,11,4) rot=(1,0,0;1.5708rad)
  Radius = 1.5
FEATURE [Part::Cylinder] Cylinder138  label="Cylinder226"
  Angle = 360
  AttacherType = Attacher::AttachEngine3D
  Height = 14
  Placement = pos=(-28,11,4) rot=(1,0,0;1.5708rad)
  Radius = 1.5
FEATURE [Part::Fuse] Fusion166  label="Wheel Mount Holes"
  Base = -> Cylinder137
  Tool = -> Cylinder138
FEATURE [Part::Cut] Cut045060  label="Wheel Mount"
  Base = -> Cut045059
  Tool = -> Fusion165
FEATURE [Part::Box] Box014032  label="Motor Mount Right002"
  AttacherType = Attacher::AttachEngine3D
  Height = 16
  Length = 4
  Placement = pos=(-46,-13,7) rot=(0,0,1;0rad)
  Width = 20
FEATURE [Part::Cylinder] Cylinder139  label="Cylinder227"
  Angle = 360
  AttacherType = Attacher::AttachEngine3D
  Height = 10
  Placement = pos=(0,18,29) rot=(0,0,1;0rad)
  Radius = 2.25
FEATURE [Part::Cylinder] Cylinder140  label="Cylinder228"
  Angle = 360
  AttacherType = Attacher::AttachEngine3D
  Height = 10
  Placement = pos=(4.5,18,32) rot=(0,0,1;0rad)
  Radius = 1
FEATURE [Part::Cylinder] Cylinder141  label="Cylinder229"
  Angle = 360
  AttacherType = Attacher::AttachEngine3D
  Height = 10
  Placement = pos=(-4.5,18,32) rot=(0,0,1;0rad)
  Radius = 1
FEATURE [Part::Fuse] Fusion169  label="Mounting Screw Holes004"
  Base = -> Cylinder140
  Tool = -> Cylinder141
FEATURE [Part::Fuse] Fusion170  label="Motor Holes Right002"
  Base = -> Cylinder139
  Placement = pos=(-79,-7,-3) rot=(0.57735,0.57735,0.57735;2.0944rad)
  Tool = -> Fusion169
FEATURE [Part::Box] Box014033  label="Cube070"
  AttacherType = Attacher::AttachEngine3D
  Height = 23
  Length = 22
  Placement = pos=(-46,4,0) rot=(0,0,1;0rad)
  Width = 3
FEATURE [Part::Fuse] Fusion168
  Base = -> Box014032
  Tool = -> Box014033
FEATURE [Part::Cut] Cut045062
  Base = -> Fusion168
  Tool = -> Fusion170
FEATURE [Part::Cylinder] Cylinder142  label="Cylinder230"
  Angle = 360
  AttacherType = Attacher::AttachEngine3D
  Height = 14
  Placement = pos=(-38,11,4) rot=(1,0,0;1.5708rad)
  Radius = 1.5
FEATURE [Part::Cylinder] Cylinder143  label="Cylinder231"
  Angle = 360
  AttacherType = Attacher::AttachEngine3D
  Height = 14
  Placement = pos=(-28,11,4) rot=(1,0,0;1.5708rad)
  Radius = 1.5
FEATURE [Part::Fuse] Fusion167
  Base = -> Cylinder142
  Tool = -> Cylinder143
FEATURE [Part::Cut] Cut045061  label="Wheel Mount001"
  Base = -> Cut045062
  Tool = -> Fusion167
FEATURE [App::DocumentObjectGroup] Group  label="Older version parts"
  Group = -> [Compound,Compound001,Compound002,Cylinder064,Cylinder010,Cylinder011,Fusion096,Part__Mirroring,Fusion054,Part__Mirroring004,Cut014,Cut015,Cut016,Cut017,Box012,Box013,Part__Mirroring005,Box010,Cut045061,Part__Mirroring003,Part__Mirroring014]
FEATURE [Part::Fillet] Fillet020
  Base = -> Cut045060
  Edges = 1 edges r=3: [Edge35]
FEATURE [Part::Fillet] Fillet021
  Base = -> Fillet020
  Edges = 1 edges r=6: [Edge11]
FEATURE [Part::Fillet] Fillet022
  Base = -> Fillet021
  Edges = 1 edges r=1: [Edge6]
FEATURE [Part::Fillet] Fillet023  label="Wheel Mount003"
  Base = -> Fillet022
  Edges = 1 edges r=1: [Edge6]
FEATURE [Part::Box] Box014034  label="Motor Mount Right003"
  AttacherType = Attacher::AttachEngine3D
  Height = 16
  Length = 4
  Placement = pos=(-46,-13,7) rot=(0,0,1;0rad)
  Width = 20
FEATURE [Part::Cylinder] Cylinder144  label="Cylinder232"
  Angle = 360
  AttacherType = Attacher::AttachEngine3D
  Height = 10
  Placement = pos=(0,18,29) rot=(0,0,1;0rad)
  Radius = 2.25
FEATURE [Part::Cylinder] Cylinder145  label="Cylinder233"
  Angle = 360
  AttacherType = Attacher::AttachEngine3D
  Height = 10
  Placement = pos=(4.5,18,32) rot=(0,0,1;0rad)
  Radius = 1
FEATURE [Part::Cylinder] Cylinder146  label="Cylinder234"
  Angle = 360
  AttacherType = Attacher::AttachEngine3D
  Height = 10
  Placement = pos=(-4.5,18,32) rot=(0,0,1;0rad)
  Radius = 1
FEATURE [Part::Fuse] Fusion173  label="Mounting Screw Holes005"
  Base = -> Cylinder145
  Tool = -> Cylinder146
FEATURE [Part::Fuse] Fusion174  label="Motor Holes Right003"
  Base = -> Cylinder144
  Placement = pos=(-79,-7,-3) rot=(0.57735,0.57735,0.57735;2.0944rad)
  Tool = -> Fusion173
FEATURE [Part::Box] Box014035  label="Cube071"
  AttacherType = Attacher::AttachEngine3D
  Height = 23
  Length = 22
  Placement = pos=(-46,4,0) rot=(0,0,1;0rad)
  Width = 3
FEATURE [Part::Fuse] Fusion172
  Base = -> Box014034
  Tool = -> Box014035
FEATURE [Part::Cut] Cut045064
  Base = -> Fusion172
  Tool = -> Fusion174
FEATURE [Part::Cylinder] Cylinder147  label="Cylinder235"
  Angle = 360
  AttacherType = Attacher::AttachEngine3D
  Height = 14
  Placement = pos=(-38,11,4) rot=(1,0,0;1.5708rad)
  Radius = 1.5
FEATURE [Part::Cylinder] Cylinder148  label="Cylinder236"
  Angle = 360
  AttacherType = Attacher::AttachEngine3D
  Height = 14
  Placement = pos=(-28,11,4) rot=(1,0,0;1.5708rad)
  Radius = 1.5
FEATURE [Part::Fuse] Fusion171
  Base = -> Cylinder147
  Tool = -> Cylinder148
FEATURE [Part::Cut] Cut045063  label="Wheel Mount002"
  Base = -> Cut045064
  Tool = -> Fusion171
FEATURE [Part::Fillet] Fillet026
  Base = -> Cut045063
  Edges = 1 edges r=3: [Edge35]
FEATURE [Part::Fillet] Fillet027
  Base = -> Fillet026
  Edges = 1 edges r=6: [Edge11]
FEATURE [Part::Fillet] Fillet025
  Base = -> Fillet027
  Edges = 1 edges r=1: [Edge6]
FEATURE [Part::Fillet] Fillet024
  Base = -> Fillet025
  Edges = 1 edges r=1: [Edge6]
FEATURE [Part::Mirroring] Part__Mirroring015  label="WheelMount Mirror"
  Base = (0,0,0)
  Normal = (1,0,0)
  Placement = pos=(27,0,0) rot=(0,0,1;0rad)
  Source = -> Fillet024
FEATURE [Part::MultiFuse] Fusion175  label="Arduino Mount Holes"
  Shapes = -> [Cylinder115,Cylinder116,Cylinder117,Cylinder118]
FEATURE [Part::MultiFuse] Fusion176  label="Base Cube"
  Shapes = -> [Box016,Box017,Box015]
FEATURE [Part::Cylinder] Cylinder149  label="Sensor Mount Hole 2"
  Angle = 360
  AttacherType = Attacher::AttachEngine3D
  Height = 14
  Placement = pos=(66,11,-22) rot=(1,0,0;1.5708rad)
  Radius = 1.5
FEATURE [Part::Cylinder] Cylinder150  label="Cylinder238"
  Angle = 360
  AttacherType = Attacher::AttachEngine3D
  Height = 14
  Placement = pos=(-38,11,4) rot=(1,0,0;1.5708rad)
  Radius = 1.5
FEATURE [Part::Cylinder] Cylinder151  label="Cylinder239"
  Angle = 360
  AttacherType = Attacher::AttachEngine3D
  Height = 14
  Placement = pos=(-28,11,4) rot=(1,0,0;1.5708rad)
  Radius = 1.5
FEATURE [Part::Fuse] Fusion177  label="Wheel Mount Holes001"
  Base = -> Cylinder150
  Placement = pos=(93,0,0) rot=(0,0,1;0rad)
  Tool = -> Cylinder151
FEATURE [Part::Fuse] Fusion178  label="Sensor Mount Holes"
  Base = -> Cylinder129
  Tool = -> Cylinder149
FEATURE [Part::Fuse] Fusion179
  Base = -> Cut045053
  Tool = -> Fusion176
FEATURE [Part::Cut] Cut045065
  Base = -> Fusion179
  Tool = -> Fusion178
FEATURE [Part::Cut] Cut045066
  Base = -> Cut045065
  Tool = -> Fusion177
FEATURE [Part::Cut] Cut045067
  Base = -> Cut045066
  Tool = -> Fusion175
FEATURE [Part::Cut] Cut045068
  Base = -> Cut045067
  Tool = -> Fusion166
FEATURE [Part::Cut] Cut045069
  Base = -> Cut045068
  Tool = -> Fusion057
FEATURE [Part::Cut] Cut045070
  Base = -> Cut045069
  Tool = -> Fusion058
FEATURE [Part::MultiFuse] Fusion180
  Shapes = -> [Cut045049,Cut045050,Cut045051,Cut045052]
FEATURE [Part::Cut] Cut045071
  Base = -> Cut045070
  Tool = -> Fusion180
FEATURE [Part::Chamfer] Chamfer011
  Base = -> Cut045071
  Edges = 1 edges r=30: [Edge139]
FEATURE [Part::Chamfer] Chamfer012
  Base = -> Chamfer011
  Edges = 1 edges r=30: [Edge125]
FEATURE [Part::Chamfer] Chamfer013
  Base = -> Chamfer012
  Edges = 1 edges r=25: [Edge37]
FEATURE [Part::Chamfer] Chamfer014
  Base = -> Chamfer013
  Edges = 1 edges r=25: [Edge125]
FEATURE [Part::MultiFuse] Fusion181
  Shapes = -> [Cylinder123,Cylinder124,Part__Mirroring012,Part__Mirroring013]
FEATURE [Part::Cut] Cut045072
  Base = -> Chamfer014
  Tool = -> Fusion181
FEATURE [Part::Chamfer] Chamfer015
  Base = -> Cut045072
  Edges = 1 edges r=1.5: [Edge16]
FEATURE [Part::Chamfer] Chamfer016
  Base = -> Chamfer015
  Edges = 1 edges r=1.5: [Edge17]
FEATURE [Part::Chamfer] Chamfer017
  Base = -> Chamfer016
  Edges = 1 edges r=1.5: [Edge114]
FEATURE [Part::Chamfer] Chamfer018
  Base = -> Chamfer017
  Edges = 1 edges r=1.5: [Edge12]
FEATURE [Part::Chamfer] Chamfer019
  Base = -> Chamfer018
  Edges = 1 edges r=2: [Edge107]
FEATURE [Part::Chamfer] Chamfer020
  Base = -> Chamfer019
  Edges = 1 edges r=2: [Edge14]
FEATURE [Part::Chamfer] Chamfer021
  Base = -> Chamfer020
  Edges = 1 edges r=2: [Edge15]
FEATURE [Part::Chamfer] Chamfer022
  Base = -> Chamfer021
  Edges = 1 edges r=2: [Edge120]
FEATURE [Part::Chamfer] Chamfer023
  Base = -> Chamfer022
  Edges = 1 edges r=2: [Edge12]
FEATURE [Part::Chamfer] Chamfer024
  Base = -> Chamfer023
  Edges = 1 edges r=2: [Edge12]
FEATURE [Part::Cylinder] Cylinder152  label="Cylinder240"
  Angle = 360
  AttacherType = Attacher::AttachEngine3D
  Height = 10
  Placement = pos=(-39,9,-25) rot=(1,0,0;1.5708rad)
  Radius = 3
FEATURE [Part::Cut] Cut045073
  Base = -> Cut045054
  Tool = -> Cylinder152
FEATURE [Part::Box] Box014036  label="Cube072"
  AttacherType = Attacher::AttachEngine3D
  Height = 4
  Length = 6
  Placement = pos=(-42,0,-25.5) rot=(0,0,1;0rad)
  Width = 10
FEATURE [Part::Cut] Cut045074
  Base = -> Cut045073
  Tool = -> Box014036
FEATURE [Part::Fuse] Fusion182
  Base = -> Fusion154
  Tool = -> Cut045074
FEATURE [Part::Fuse] Fusion183
  Base = -> Fusion152
  Tool = -> Fusion182
FEATURE [Part::Cut] Cut045075
  Base = -> Fusion183
  Tool = -> Fusion153
FEATURE [Part::Chamfer] Chamfer
  Base = -> Cut045075
  Edges = 1 edges r=6.99: [Edge15]
FEATURE [Part::Fillet] Fillet028
  Base = -> Chamfer
  Edges = 1 edges r=1: [Edge51]
FEATURE [Part::Fillet] Fillet029
  Base = -> Fillet028
  Edges = 1 edges r=1: [Edge6]
FEATURE [Part::Fillet] Fillet030
  Base = -> Fillet029
  Edges = 1 edges r=8: [Edge80]
FEATURE [Part::Fillet] Fillet031
  Base = -> Fillet030
  Edges = 1 edges r=6: [Edge23]
FEATURE [Part::Fillet] Fillet032  label="Sensor Mount"
  Base = -> Fillet031
  Edges = 1 edges r=1: [Edge38]
